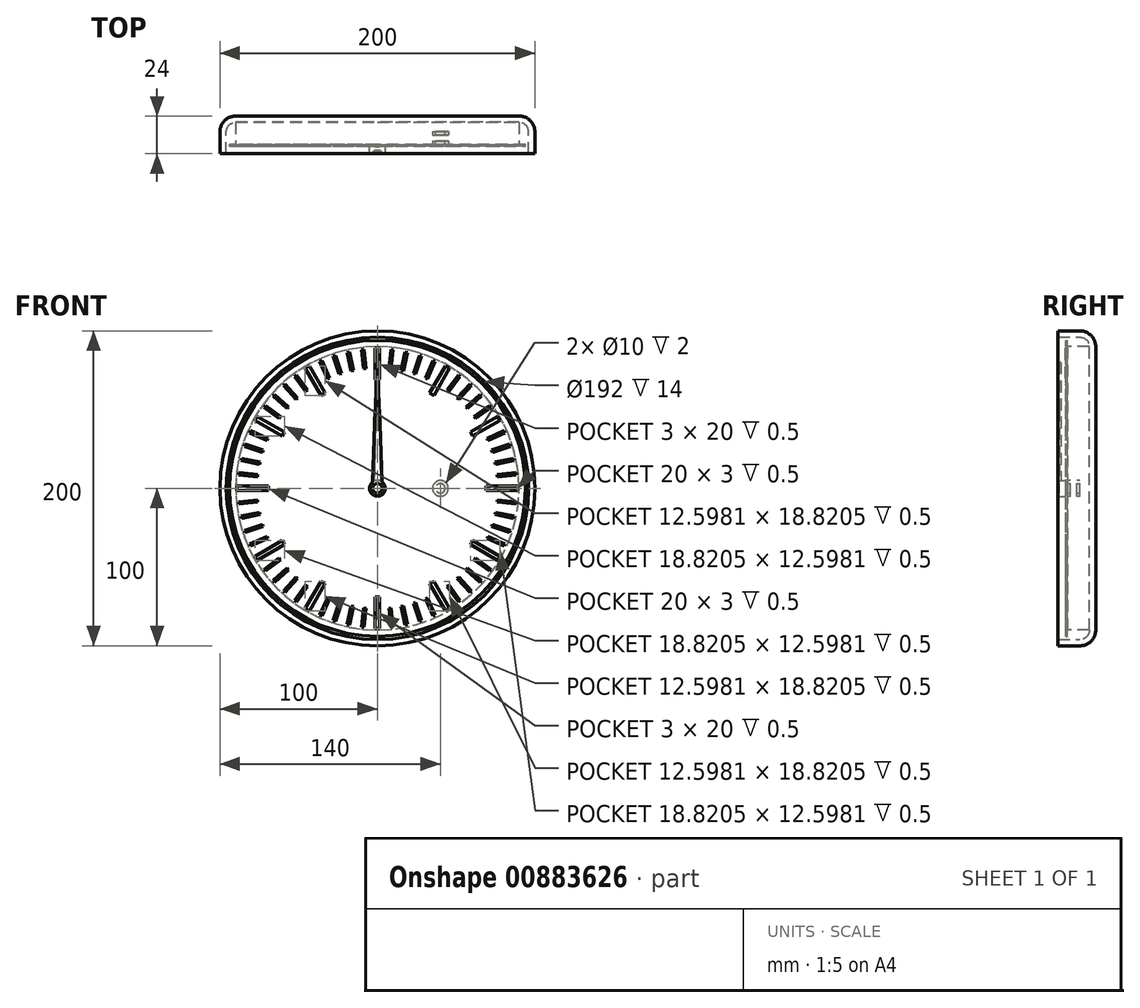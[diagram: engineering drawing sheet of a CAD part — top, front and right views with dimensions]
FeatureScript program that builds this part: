
annotation { "Feature Type Name" : "Feature", "Feature Type Description" : "" }
export const myFeature = defineFeature(function(context is Context, id is Id, definition is map)
    precondition{}
    {
        {
            var Q0;
            Q0=qCreatedBy(makeId("Front.planeOp"),FACE);
            var sketch = newSketch(context, id + "F0", { "sketchPlane" : qUnion([Q0])});
            skCircle(sketch, "E0", {"center": v(0, 0) * mm, "radius": 100 * mm});
            skSolve(sketch);
        }
        {
            var Q0;
            Q0 = qSketchRegion(id + "F0", true);
            extrude(context, id + "F1", {"entities" : qUnion([Q0]), "depth" : 24 * mm, "offsetDistance" : 25 * mm});
        }
        {
            var Q0;
            Q0=makeQuery(id+"F1.opExtrude","CAP_EDGE",EDGE,{"disambiguationData":[OSD([sQuery(id+"F0.wireOp",EDGE,"E0")])],"isStart":true});
            fillet(context, id + "F2", {"entities" : qUnion([Q0]), "radius" : 10 * mm, "tangentPropagation" : true, "allowEdgeOverflow" : false});
        }
        {
            var Q0;
            Q0=makeQuery(id+"F1.opExtrude","CAP_FACE",FACE,{"disambiguationData":[OSD([sQuery(id+"F0.wireOp",EDGE,"E0")])],"isStart":false});
            shell(context, id + "F3", {"entities" : qUnion([Q0]), "thickness" : 4 * mm});
        }
        {
            var Q0;
            {var subQ0=sQuery(id+"F0.wireOp",EDGE,"E0");Q0=makeQuery(id+"F3.opShell","OFFSET_FACE",FACE,{"disambiguationData":[OSD([subQ0]),TDD([makeQuery(id+"F1.opExtrude","CAP_FACE",FACE,{"disambiguationData":[OSD([subQ0])],"isStart":true})])]});}
            var sketch = newSketch(context, id + "F4", { "sketchPlane" : qUnion([Q0])});
            skCircle(sketch, "E1", {"center": v(0, 0) * mm, "radius": 5 * mm});
            skCircle(sketch, "E2", {"center": v(40, 0) * mm, "radius": 5 * mm});
            skCircle(sketch, "E3", {"center": v(0, 0) * mm, "radius": 3 * mm});
            skCircle(sketch, "E4", {"center": v(40, 0) * mm, "radius": 3 * mm});
            skSolve(sketch);
        }
        {
            var Q0;
            Q0 = qSketchRegion(id + "F4", true);
            extrude(context, id + "F5", {"entities" : qUnion([Q0]), "operationType" : NewBodyOperationType.ADD, "depth" : 2 * mm, "offsetDistance" : 25 * mm});
        }
        {
            var Q0;
            {var subQ0=sQuery(id+"F0.wireOp",EDGE,"E0");Q0=makeQuery(id+"F5.boolean.opBoolean","SPLIT",FACE,{"disambiguationData":[TD([makeQuery(id+"F5.opExtrude","SWEPT_FACE",FACE,{"disambiguationData":[OSD([sQuery(id+"F4.wireOp",EDGE,"E3")])]})])],"derivedFrom":makeQuery(id+"F3.opShell","OFFSET_FACE",FACE,{"disambiguationData":[OSD([subQ0]),TDD([makeQuery(id+"F1.opExtrude","CAP_FACE",FACE,{"disambiguationData":[OSD([subQ0])],"isStart":true})])]})});}
            extrude(context, id + "F6", {"entities" : qUnion([Q0]), "depth" : 19 * mm, "offsetDistance" : 25 * mm});
        }
        {
            var Q0;
            {var subQ0=sQuery(id+"F0.wireOp",EDGE,"E0");Q0=makeQuery(id+"F5.boolean.opBoolean","SPLIT",FACE,{"disambiguationData":[TD([makeQuery(id+"F5.opExtrude","SWEPT_FACE",FACE,{"disambiguationData":[OSD([sQuery(id+"F4.wireOp",EDGE,"E4")])]})])],"derivedFrom":makeQuery(id+"F3.opShell","OFFSET_FACE",FACE,{"disambiguationData":[OSD([subQ0]),TDD([makeQuery(id+"F1.opExtrude","CAP_FACE",FACE,{"disambiguationData":[OSD([subQ0])],"isStart":true})])]})});}
            extrude(context, id + "F7", {"entities" : qUnion([Q0]), "depth" : 8 * mm, "offsetDistance" : 25 * mm});
        }
        {
            var Q0;
            Q0=makeQuery(id+"F5.opExtrude","CAP_FACE",FACE,{"disambiguationData":[OSD([sQuery(id+"F4.wireOp",EDGE,"E1"),sQuery(id+"F4.wireOp",EDGE,"E3")])],"isStart":false});
            var sketch = newSketch(context, id + "F8", { "sketchPlane" : qUnion([Q0])});
            skCircle(sketch, "E5", {"center": v(0, 0) * mm, "radius": 9.38 * mm});
            skLineSegment(sketch, "E6", {"start": v(0, 11.38) * mm, "end": v(1.18, 11.38) * mm});
            skLineSegment(sketch, "E7", {"start": v(1.18, 11.38) * mm, "end": v(1.55, 9.25) * mm});
            skLineSegment(sketch, "E8.MirrorCS", {"start": v(0, 11.38) * mm, "end": v(-1.18, 11.38) * mm});
            skLineSegment(sketch, "E9.MirrorCS", {"start": v(-1.18, 11.38) * mm, "end": v(-1.55, 9.25) * mm});
            skLineSegment(sketch, "E10.1.0", {"start": v(-7.64, 8.51) * mm, "end": v(-6.7, 6.57) * mm});
            skLineSegment(sketch, "E10.1.1", {"start": v(-6.69, 9.2) * mm, "end": v(-7.64, 8.51) * mm});
            skLineSegment(sketch, "E10.1.2", {"start": v(-6.69, 9.2) * mm, "end": v(-5.73, 9.9) * mm});
            skLineSegment(sketch, "E10.1.3", {"start": v(-5.73, 9.9) * mm, "end": v(-4.18, 8.4) * mm});
            skLineSegment(sketch, "E10.2.0", {"start": v(-11.18, 2.4) * mm, "end": v(-9.27, 1.38) * mm});
            skLineSegment(sketch, "E10.2.1", {"start": v(-10.82, 3.52) * mm, "end": v(-11.18, 2.4) * mm});
            skLineSegment(sketch, "E10.2.2", {"start": v(-10.82, 3.52) * mm, "end": v(-10.45, 4.64) * mm});
            skLineSegment(sketch, "E10.2.3", {"start": v(-10.45, 4.64) * mm, "end": v(-8.31, 4.33) * mm});
            skLineSegment(sketch, "E11.2.3.0", {"start": v(-10.45, -4.64) * mm, "end": v(-8.31, -4.33) * mm});
            skLineSegment(sketch, "E11.3.3.0", {"start": v(-10.82, -3.52) * mm, "end": v(-10.45, -4.64) * mm});
            skLineSegment(sketch, "E11.6.3.0", {"start": v(-10.82, -3.52) * mm, "end": v(-11.18, -2.4) * mm});
            skLineSegment(sketch, "E11.9.3.0", {"start": v(-11.18, -2.4) * mm, "end": v(-9.27, -1.38) * mm});
            skLineSegment(sketch, "E11.2.4.0", {"start": v(-5.73, -9.9) * mm, "end": v(-4.18, -8.4) * mm});
            skLineSegment(sketch, "E11.3.4.0", {"start": v(-6.69, -9.2) * mm, "end": v(-5.73, -9.9) * mm});
            skLineSegment(sketch, "E11.6.4.0", {"start": v(-6.69, -9.2) * mm, "end": v(-7.64, -8.51) * mm});
            skLineSegment(sketch, "E11.9.4.0", {"start": v(-7.64, -8.51) * mm, "end": v(-6.7, -6.57) * mm});
            skLineSegment(sketch, "E11.2.5.0", {"start": v(1.18, -11.38) * mm, "end": v(1.55, -9.25) * mm});
            skLineSegment(sketch, "E11.3.5.0", {"start": v(0, -11.38) * mm, "end": v(1.18, -11.38) * mm});
            skLineSegment(sketch, "E11.6.5.0", {"start": v(0, -11.38) * mm, "end": v(-1.18, -11.38) * mm});
            skLineSegment(sketch, "E11.9.5.0", {"start": v(-1.18, -11.38) * mm, "end": v(-1.55, -9.25) * mm});
            skLineSegment(sketch, "E11.2.6.0", {"start": v(7.64, -8.51) * mm, "end": v(6.7, -6.57) * mm});
            skLineSegment(sketch, "E11.3.6.0", {"start": v(6.69, -9.2) * mm, "end": v(7.64, -8.51) * mm});
            skLineSegment(sketch, "E11.6.6.0", {"start": v(6.69, -9.2) * mm, "end": v(5.73, -9.9) * mm});
            skLineSegment(sketch, "E11.9.6.0", {"start": v(5.73, -9.9) * mm, "end": v(4.18, -8.4) * mm});
            skLineSegment(sketch, "E11.2.7.0", {"start": v(11.18, -2.4) * mm, "end": v(9.27, -1.38) * mm});
            skLineSegment(sketch, "E11.3.7.0", {"start": v(10.82, -3.52) * mm, "end": v(11.18, -2.4) * mm});
            skLineSegment(sketch, "E11.6.7.0", {"start": v(10.82, -3.52) * mm, "end": v(10.45, -4.64) * mm});
            skLineSegment(sketch, "E11.9.7.0", {"start": v(10.45, -4.64) * mm, "end": v(8.31, -4.33) * mm});
            skLineSegment(sketch, "E11.2.8.0", {"start": v(10.45, 4.64) * mm, "end": v(8.31, 4.33) * mm});
            skLineSegment(sketch, "E11.3.8.0", {"start": v(10.82, 3.52) * mm, "end": v(10.45, 4.64) * mm});
            skLineSegment(sketch, "E11.6.8.0", {"start": v(10.82, 3.52) * mm, "end": v(11.18, 2.4) * mm});
            skLineSegment(sketch, "E11.9.8.0", {"start": v(11.18, 2.4) * mm, "end": v(9.27, 1.38) * mm});
            skLineSegment(sketch, "E11.2.9.0", {"start": v(5.73, 9.9) * mm, "end": v(4.18, 8.4) * mm});
            skLineSegment(sketch, "E11.3.9.0", {"start": v(6.69, 9.2) * mm, "end": v(5.73, 9.9) * mm});
            skLineSegment(sketch, "E11.6.9.0", {"start": v(6.69, 9.2) * mm, "end": v(7.64, 8.51) * mm});
            skLineSegment(sketch, "E11.9.9.0", {"start": v(7.64, 8.51) * mm, "end": v(6.7, 6.57) * mm});
            skSolve(sketch);
        }
        {
            var Q0;
            Q0 = qSketchRegion(id + "F8", true);
            extrude(context, id + "F9", {"entities" : qUnion([Q0]), "operationType" : NewBodyOperationType.ADD, "depth" : 4 * mm, "offsetDistance" : 25 * mm});
        }
        {
            var Q0;
            Q0=makeQuery(id+"F5.opExtrude","CAP_FACE",FACE,{"disambiguationData":[OSD([sQuery(id+"F4.wireOp",EDGE,"E2"),sQuery(id+"F4.wireOp",EDGE,"E4")])],"isStart":false});
            var sketch = newSketch(context, id + "F10", { "sketchPlane" : qUnion([Q0])});
            skCircle(sketch, "E12", {"center": v(40, 0) * mm, "radius": 28.12 * mm});
            skLineSegment(sketch, "E13", {"start": v(9.88, 0) * mm, "end": v(9.88, 1.18) * mm});
            skLineSegment(sketch, "E14", {"start": v(9.88, 1.18) * mm, "end": v(11.92, 1.54) * mm});
            skLineSegment(sketch, "E15.MirrorCS", {"start": v(9.88, 0) * mm, "end": v(9.88, -1.18) * mm});
            skLineSegment(sketch, "E16.MirrorCS", {"start": v(9.88, -1.18) * mm, "end": v(11.92, -1.54) * mm});
            skLineSegment(sketch, "E17.1.0", {"start": v(10.78, -7.42) * mm, "end": v(12.85, -7.34) * mm});
            skLineSegment(sketch, "E17.1.1", {"start": v(10.53, -6.26) * mm, "end": v(10.78, -7.42) * mm});
            skLineSegment(sketch, "E17.1.2", {"start": v(10.53, -6.26) * mm, "end": v(10.29, -5.11) * mm});
            skLineSegment(sketch, "E17.1.3", {"start": v(10.29, -5.11) * mm, "end": v(12.21, -4.33) * mm});
            skLineSegment(sketch, "E17.2.0", {"start": v(12.96, -13.33) * mm, "end": v(14.97, -12.83) * mm});
            skLineSegment(sketch, "E17.2.1", {"start": v(12.48, -12.25) * mm, "end": v(12.96, -13.33) * mm});
            skLineSegment(sketch, "E17.2.2", {"start": v(12.48, -12.25) * mm, "end": v(12, -11.18) * mm});
            skLineSegment(sketch, "E17.2.3", {"start": v(12, -11.18) * mm, "end": v(13.72, -10.02) * mm});
            skLineSegment(sketch, "E18.1.3.0", {"start": v(16.32, -18.66) * mm, "end": v(18.18, -17.75) * mm});
            skLineSegment(sketch, "E18.3.3.0", {"start": v(15.63, -17.7) * mm, "end": v(16.32, -18.66) * mm});
            skLineSegment(sketch, "E18.6.3.0", {"start": v(15.63, -17.7) * mm, "end": v(14.94, -16.75) * mm});
            skLineSegment(sketch, "E18.9.3.0", {"start": v(14.94, -16.75) * mm, "end": v(16.38, -15.26) * mm});
            skLineSegment(sketch, "E18.1.4.0", {"start": v(20.72, -23.18) * mm, "end": v(22.35, -21.9) * mm});
            skLineSegment(sketch, "E18.3.4.0", {"start": v(19.84, -22.39) * mm, "end": v(20.72, -23.18) * mm});
            skLineSegment(sketch, "E18.6.4.0", {"start": v(19.84, -22.39) * mm, "end": v(18.97, -21.6) * mm});
            skLineSegment(sketch, "E18.9.4.0", {"start": v(18.97, -21.6) * mm, "end": v(20.07, -19.84) * mm});
            skLineSegment(sketch, "E18.1.5.0", {"start": v(25.96, -26.68) * mm, "end": v(27.3, -25.09) * mm});
            skLineSegment(sketch, "E18.3.5.0", {"start": v(24.94, -26.09) * mm, "end": v(25.96, -26.68) * mm});
            skLineSegment(sketch, "E18.6.5.0", {"start": v(24.94, -26.09) * mm, "end": v(23.92, -25.5) * mm});
            skLineSegment(sketch, "E18.9.5.0", {"start": v(23.92, -25.5) * mm, "end": v(24.63, -23.55) * mm});
            skLineSegment(sketch, "E18.1.6.0", {"start": v(31.81, -29.01) * mm, "end": v(32.78, -27.18) * mm});
            skLineSegment(sketch, "E18.3.6.0", {"start": v(30.7, -28.65) * mm, "end": v(31.81, -29.01) * mm});
            skLineSegment(sketch, "E18.6.6.0", {"start": v(30.7, -28.65) * mm, "end": v(29.57, -28.29) * mm});
            skLineSegment(sketch, "E18.9.6.0", {"start": v(29.57, -28.29) * mm, "end": v(29.86, -26.23) * mm});
            skLineSegment(sketch, "E18.1.7.0", {"start": v(38.02, -30.08) * mm, "end": v(38.6, -28.09) * mm});
            skLineSegment(sketch, "E18.3.7.0", {"start": v(36.85, -29.96) * mm, "end": v(38.02, -30.08) * mm});
            skLineSegment(sketch, "E18.6.7.0", {"start": v(36.85, -29.96) * mm, "end": v(35.68, -29.84) * mm});
            skLineSegment(sketch, "E18.9.7.0", {"start": v(35.68, -29.84) * mm, "end": v(35.53, -27.77) * mm});
            skLineSegment(sketch, "E18.1.8.0", {"start": v(44.32, -29.84) * mm, "end": v(44.47, -27.77) * mm});
            skLineSegment(sketch, "E18.3.8.0", {"start": v(43.15, -29.96) * mm, "end": v(44.32, -29.84) * mm});
            skLineSegment(sketch, "E18.6.8.0", {"start": v(43.15, -29.96) * mm, "end": v(41.98, -30.08) * mm});
            skLineSegment(sketch, "E18.9.8.0", {"start": v(41.98, -30.08) * mm, "end": v(41.4, -28.09) * mm});
            skLineSegment(sketch, "E18.1.9.0", {"start": v(50.43, -28.29) * mm, "end": v(50.14, -26.23) * mm});
            skLineSegment(sketch, "E18.3.9.0", {"start": v(49.3, -28.65) * mm, "end": v(50.43, -28.29) * mm});
            skLineSegment(sketch, "E18.6.9.0", {"start": v(49.3, -28.65) * mm, "end": v(48.19, -29.01) * mm});
            skLineSegment(sketch, "E18.9.9.0", {"start": v(48.19, -29.01) * mm, "end": v(47.22, -27.18) * mm});
            skLineSegment(sketch, "E18.1.10.0", {"start": v(56.08, -25.5) * mm, "end": v(55.37, -23.55) * mm});
            skLineSegment(sketch, "E18.3.10.0", {"start": v(55.06, -26.09) * mm, "end": v(56.08, -25.5) * mm});
            skLineSegment(sketch, "E18.6.10.0", {"start": v(55.06, -26.09) * mm, "end": v(54.04, -26.68) * mm});
            skLineSegment(sketch, "E18.9.10.0", {"start": v(54.04, -26.68) * mm, "end": v(52.7, -25.09) * mm});
            skLineSegment(sketch, "E18.1.11.0", {"start": v(61.03, -21.6) * mm, "end": v(59.93, -19.84) * mm});
            skLineSegment(sketch, "E18.3.11.0", {"start": v(60.16, -22.39) * mm, "end": v(61.03, -21.6) * mm});
            skLineSegment(sketch, "E18.6.11.0", {"start": v(60.16, -22.39) * mm, "end": v(59.28, -23.18) * mm});
            skLineSegment(sketch, "E18.9.11.0", {"start": v(59.28, -23.18) * mm, "end": v(57.65, -21.9) * mm});
            skLineSegment(sketch, "E18.1.12.0", {"start": v(65.06, -16.75) * mm, "end": v(63.62, -15.26) * mm});
            skLineSegment(sketch, "E18.3.12.0", {"start": v(64.37, -17.7) * mm, "end": v(65.06, -16.75) * mm});
            skLineSegment(sketch, "E18.6.12.0", {"start": v(64.37, -17.7) * mm, "end": v(63.68, -18.66) * mm});
            skLineSegment(sketch, "E18.9.12.0", {"start": v(63.68, -18.66) * mm, "end": v(61.82, -17.75) * mm});
            skLineSegment(sketch, "E18.1.13.0", {"start": v(68, -11.18) * mm, "end": v(66.28, -10.02) * mm});
            skLineSegment(sketch, "E18.3.13.0", {"start": v(67.52, -12.25) * mm, "end": v(68, -11.18) * mm});
            skLineSegment(sketch, "E18.6.13.0", {"start": v(67.52, -12.25) * mm, "end": v(67.04, -13.33) * mm});
            skLineSegment(sketch, "E18.9.13.0", {"start": v(67.04, -13.33) * mm, "end": v(65.03, -12.83) * mm});
            skLineSegment(sketch, "E18.1.14.0", {"start": v(69.71, -5.11) * mm, "end": v(67.79, -4.33) * mm});
            skLineSegment(sketch, "E18.3.14.0", {"start": v(69.47, -6.26) * mm, "end": v(69.71, -5.11) * mm});
            skLineSegment(sketch, "E18.6.14.0", {"start": v(69.47, -6.26) * mm, "end": v(69.22, -7.42) * mm});
            skLineSegment(sketch, "E18.9.14.0", {"start": v(69.22, -7.42) * mm, "end": v(67.15, -7.34) * mm});
            skLineSegment(sketch, "E18.1.15.0", {"start": v(70.13, 1.18) * mm, "end": v(68.08, 1.54) * mm});
            skLineSegment(sketch, "E18.3.15.0", {"start": v(70.12, 0) * mm, "end": v(70.12, 1.18) * mm});
            skLineSegment(sketch, "E18.6.15.0", {"start": v(70.12, 0) * mm, "end": v(70.12, -1.18) * mm});
            skLineSegment(sketch, "E18.9.15.0", {"start": v(70.13, -1.18) * mm, "end": v(68.08, -1.54) * mm});
            skLineSegment(sketch, "E18.1.16.0", {"start": v(69.22, 7.42) * mm, "end": v(67.15, 7.34) * mm});
            skLineSegment(sketch, "E18.3.16.0", {"start": v(69.47, 6.26) * mm, "end": v(69.22, 7.42) * mm});
            skLineSegment(sketch, "E18.6.16.0", {"start": v(69.47, 6.26) * mm, "end": v(69.71, 5.11) * mm});
            skLineSegment(sketch, "E18.9.16.0", {"start": v(69.71, 5.11) * mm, "end": v(67.79, 4.33) * mm});
            skLineSegment(sketch, "E18.1.17.0", {"start": v(67.04, 13.33) * mm, "end": v(65.03, 12.83) * mm});
            skLineSegment(sketch, "E18.3.17.0", {"start": v(67.52, 12.25) * mm, "end": v(67.04, 13.33) * mm});
            skLineSegment(sketch, "E18.6.17.0", {"start": v(67.52, 12.25) * mm, "end": v(68, 11.18) * mm});
            skLineSegment(sketch, "E18.9.17.0", {"start": v(68, 11.18) * mm, "end": v(66.28, 10.02) * mm});
            skLineSegment(sketch, "E18.1.18.0", {"start": v(63.68, 18.66) * mm, "end": v(61.82, 17.75) * mm});
            skLineSegment(sketch, "E18.3.18.0", {"start": v(64.37, 17.7) * mm, "end": v(63.68, 18.66) * mm});
            skLineSegment(sketch, "E18.6.18.0", {"start": v(64.37, 17.7) * mm, "end": v(65.06, 16.75) * mm});
            skLineSegment(sketch, "E18.9.18.0", {"start": v(65.06, 16.75) * mm, "end": v(63.62, 15.26) * mm});
            skLineSegment(sketch, "E18.1.19.0", {"start": v(59.28, 23.18) * mm, "end": v(57.65, 21.9) * mm});
            skLineSegment(sketch, "E18.3.19.0", {"start": v(60.16, 22.39) * mm, "end": v(59.28, 23.18) * mm});
            skLineSegment(sketch, "E18.6.19.0", {"start": v(60.16, 22.39) * mm, "end": v(61.03, 21.6) * mm});
            skLineSegment(sketch, "E18.9.19.0", {"start": v(61.03, 21.6) * mm, "end": v(59.93, 19.84) * mm});
            skLineSegment(sketch, "E18.1.20.0", {"start": v(54.04, 26.68) * mm, "end": v(52.7, 25.09) * mm});
            skLineSegment(sketch, "E18.3.20.0", {"start": v(55.06, 26.09) * mm, "end": v(54.04, 26.68) * mm});
            skLineSegment(sketch, "E18.6.20.0", {"start": v(55.06, 26.09) * mm, "end": v(56.08, 25.5) * mm});
            skLineSegment(sketch, "E18.9.20.0", {"start": v(56.08, 25.5) * mm, "end": v(55.37, 23.55) * mm});
            skLineSegment(sketch, "E18.1.21.0", {"start": v(48.19, 29.01) * mm, "end": v(47.22, 27.18) * mm});
            skLineSegment(sketch, "E18.3.21.0", {"start": v(49.3, 28.65) * mm, "end": v(48.19, 29.01) * mm});
            skLineSegment(sketch, "E18.6.21.0", {"start": v(49.3, 28.65) * mm, "end": v(50.43, 28.29) * mm});
            skLineSegment(sketch, "E18.9.21.0", {"start": v(50.43, 28.29) * mm, "end": v(50.14, 26.23) * mm});
            skLineSegment(sketch, "E18.1.22.0", {"start": v(41.98, 30.08) * mm, "end": v(41.4, 28.09) * mm});
            skLineSegment(sketch, "E18.3.22.0", {"start": v(43.15, 29.96) * mm, "end": v(41.98, 30.08) * mm});
            skLineSegment(sketch, "E18.6.22.0", {"start": v(43.15, 29.96) * mm, "end": v(44.32, 29.84) * mm});
            skLineSegment(sketch, "E18.9.22.0", {"start": v(44.32, 29.84) * mm, "end": v(44.47, 27.77) * mm});
            skLineSegment(sketch, "E18.1.23.0", {"start": v(35.68, 29.84) * mm, "end": v(35.53, 27.77) * mm});
            skLineSegment(sketch, "E18.3.23.0", {"start": v(36.85, 29.96) * mm, "end": v(35.68, 29.84) * mm});
            skLineSegment(sketch, "E18.6.23.0", {"start": v(36.85, 29.96) * mm, "end": v(38.02, 30.08) * mm});
            skLineSegment(sketch, "E18.9.23.0", {"start": v(38.02, 30.08) * mm, "end": v(38.6, 28.09) * mm});
            skLineSegment(sketch, "E18.1.24.0", {"start": v(29.57, 28.29) * mm, "end": v(29.86, 26.23) * mm});
            skLineSegment(sketch, "E18.3.24.0", {"start": v(30.7, 28.65) * mm, "end": v(29.57, 28.29) * mm});
            skLineSegment(sketch, "E18.6.24.0", {"start": v(30.7, 28.65) * mm, "end": v(31.81, 29.01) * mm});
            skLineSegment(sketch, "E18.9.24.0", {"start": v(31.81, 29.01) * mm, "end": v(32.78, 27.18) * mm});
            skLineSegment(sketch, "E18.1.25.0", {"start": v(23.92, 25.5) * mm, "end": v(24.63, 23.55) * mm});
            skLineSegment(sketch, "E18.3.25.0", {"start": v(24.94, 26.09) * mm, "end": v(23.92, 25.5) * mm});
            skLineSegment(sketch, "E18.6.25.0", {"start": v(24.94, 26.09) * mm, "end": v(25.96, 26.68) * mm});
            skLineSegment(sketch, "E18.9.25.0", {"start": v(25.96, 26.68) * mm, "end": v(27.3, 25.09) * mm});
            skLineSegment(sketch, "E18.1.26.0", {"start": v(18.97, 21.6) * mm, "end": v(20.07, 19.84) * mm});
            skLineSegment(sketch, "E18.3.26.0", {"start": v(19.84, 22.39) * mm, "end": v(18.97, 21.6) * mm});
            skLineSegment(sketch, "E18.6.26.0", {"start": v(19.84, 22.39) * mm, "end": v(20.72, 23.18) * mm});
            skLineSegment(sketch, "E18.9.26.0", {"start": v(20.72, 23.18) * mm, "end": v(22.35, 21.9) * mm});
            skLineSegment(sketch, "E18.1.27.0", {"start": v(14.94, 16.75) * mm, "end": v(16.38, 15.26) * mm});
            skLineSegment(sketch, "E18.3.27.0", {"start": v(15.63, 17.7) * mm, "end": v(14.94, 16.75) * mm});
            skLineSegment(sketch, "E18.6.27.0", {"start": v(15.63, 17.7) * mm, "end": v(16.32, 18.66) * mm});
            skLineSegment(sketch, "E18.9.27.0", {"start": v(16.32, 18.66) * mm, "end": v(18.18, 17.75) * mm});
            skLineSegment(sketch, "E18.1.28.0", {"start": v(12, 11.18) * mm, "end": v(13.72, 10.02) * mm});
            skLineSegment(sketch, "E18.3.28.0", {"start": v(12.48, 12.25) * mm, "end": v(12, 11.18) * mm});
            skLineSegment(sketch, "E18.6.28.0", {"start": v(12.48, 12.25) * mm, "end": v(12.96, 13.33) * mm});
            skLineSegment(sketch, "E18.9.28.0", {"start": v(12.96, 13.33) * mm, "end": v(14.97, 12.83) * mm});
            skLineSegment(sketch, "E18.1.29.0", {"start": v(10.29, 5.11) * mm, "end": v(12.21, 4.33) * mm});
            skLineSegment(sketch, "E18.3.29.0", {"start": v(10.53, 6.26) * mm, "end": v(10.29, 5.11) * mm});
            skLineSegment(sketch, "E18.6.29.0", {"start": v(10.53, 6.26) * mm, "end": v(10.78, 7.42) * mm});
            skLineSegment(sketch, "E18.9.29.0", {"start": v(10.78, 7.42) * mm, "end": v(12.85, 7.34) * mm});
            skSolve(sketch);
        }
        {
            var Q0;
            Q0 = qSketchRegion(id + "F10", true);
            extrude(context, id + "F11", {"entities" : qUnion([Q0]), "operationType" : NewBodyOperationType.ADD, "depth" : 4 * mm, "offsetDistance" : 25 * mm});
        }
        {
            var Q0;
            Q0=makeQuery(id+"F9.opExtrude","CAP_FACE",FACE,{"disambiguationData":[OSD([sQuery(id+"F8.wireOp",EDGE,"E5"),sQuery(id+"F8.wireOp",EDGE,"E6"),sQuery(id+"F8.wireOp",EDGE,"E7"),sQuery(id+"F8.wireOp",EDGE,"E8.MirrorCS"),sQuery(id+"F8.wireOp",EDGE,"E9.MirrorCS"),sQuery(id+"F8.wireOp",EDGE,"E10.1.0"),sQuery(id+"F8.wireOp",EDGE,"E10.1.1"),sQuery(id+"F8.wireOp",EDGE,"E10.1.2"),sQuery(id+"F8.wireOp",EDGE,"E10.1.3"),sQuery(id+"F8.wireOp",EDGE,"E10.2.0"),sQuery(id+"F8.wireOp",EDGE,"E10.2.1"),sQuery(id+"F8.wireOp",EDGE,"E10.2.2"),sQuery(id+"F8.wireOp",EDGE,"E10.2.3"),sQuery(id+"F8.wireOp",EDGE,"E11.2.3.0"),sQuery(id+"F8.wireOp",EDGE,"E11.3.3.0"),sQuery(id+"F8.wireOp",EDGE,"E11.6.3.0"),sQuery(id+"F8.wireOp",EDGE,"E11.9.3.0"),sQuery(id+"F8.wireOp",EDGE,"E11.2.4.0"),sQuery(id+"F8.wireOp",EDGE,"E11.3.4.0"),sQuery(id+"F8.wireOp",EDGE,"E11.6.4.0"),sQuery(id+"F8.wireOp",EDGE,"E11.9.4.0"),sQuery(id+"F8.wireOp",EDGE,"E11.2.5.0"),sQuery(id+"F8.wireOp",EDGE,"E11.3.5.0"),sQuery(id+"F8.wireOp",EDGE,"E11.6.5.0"),sQuery(id+"F8.wireOp",EDGE,"E11.9.5.0"),sQuery(id+"F8.wireOp",EDGE,"E11.2.6.0"),sQuery(id+"F8.wireOp",EDGE,"E11.3.6.0"),sQuery(id+"F8.wireOp",EDGE,"E11.6.6.0"),sQuery(id+"F8.wireOp",EDGE,"E11.9.6.0"),sQuery(id+"F8.wireOp",EDGE,"E11.2.7.0"),sQuery(id+"F8.wireOp",EDGE,"E11.3.7.0"),sQuery(id+"F8.wireOp",EDGE,"E11.6.7.0"),sQuery(id+"F8.wireOp",EDGE,"E11.9.7.0"),sQuery(id+"F8.wireOp",EDGE,"E11.2.8.0"),sQuery(id+"F8.wireOp",EDGE,"E11.3.8.0"),sQuery(id+"F8.wireOp",EDGE,"E11.6.8.0"),sQuery(id+"F8.wireOp",EDGE,"E11.9.8.0"),sQuery(id+"F8.wireOp",EDGE,"E11.2.9.0"),sQuery(id+"F8.wireOp",EDGE,"E11.3.9.0"),sQuery(id+"F8.wireOp",EDGE,"E11.6.9.0"),sQuery(id+"F8.wireOp",EDGE,"E11.9.9.0")])],"isStart":false});
            var sketch = newSketch(context, id + "F12", { "sketchPlane" : qUnion([Q0])});
            skCircle(sketch, "E19.0", {"center": v(0, 0) * mm, "radius": 5 * mm});
            skCircle(sketch, "E19.1.0", {"center": v(0, 0) * mm, "radius": 3 * mm});
            skSolve(sketch);
        }
        {
            var Q0;
            Q0 = qSketchRegion(id + "F12", true);
            extrude(context, id + "F13", {"entities" : qUnion([Q0]), "depth" : 2 * mm, "offsetDistance" : 25 * mm});
        }
        {
            var Q0;
            Q0=makeQuery(id+"F13.opExtrude","CAP_FACE",FACE,{"disambiguationData":[OSD([sQuery(id+"F12.wireOp",EDGE,"E19.0"),sQuery(id+"F12.wireOp",EDGE,"E19.1.0")])],"isStart":false});
            var sketch = newSketch(context, id + "F14", { "sketchPlane" : qUnion([Q0])});
            skCircle(sketch, "E20", {"center": v(0, 0) * mm, "radius": 30 * mm});
            skLineSegment(sketch, "E21", {"start": v(0, 32) * mm, "end": v(0.94, 32) * mm});
            skLineSegment(sketch, "E22", {"start": v(0.94, 32) * mm, "end": v(1.3, 29.97) * mm});
            skLineSegment(sketch, "E23.MirrorCS", {"start": v(0, 32) * mm, "end": v(-0.94, 32) * mm});
            skLineSegment(sketch, "E24.MirrorCS", {"start": v(-0.94, 32) * mm, "end": v(-1.3, 29.97) * mm});
            skLineSegment(sketch, "E25.1.0", {"start": v(-5.94, 31.46) * mm, "end": v(-5.97, 29.4) * mm});
            skLineSegment(sketch, "E25.1.1", {"start": v(-5, 31.6) * mm, "end": v(-5.94, 31.46) * mm});
            skLineSegment(sketch, "E25.1.2", {"start": v(-5, 31.6) * mm, "end": v(-4.08, 31.75) * mm});
            skLineSegment(sketch, "E25.1.3", {"start": v(-4.08, 31.75) * mm, "end": v(-3.4, 29.8) * mm});
            skLineSegment(sketch, "E25.2.0", {"start": v(-10.78, 30.14) * mm, "end": v(-10.5, 28.1) * mm});
            skLineSegment(sketch, "E25.2.1", {"start": v(-9.89, 30.43) * mm, "end": v(-10.78, 30.14) * mm});
            skLineSegment(sketch, "E25.2.2", {"start": v(-9.89, 30.43) * mm, "end": v(-9, 30.73) * mm});
            skLineSegment(sketch, "E25.2.3", {"start": v(-9, 30.73) * mm, "end": v(-8.03, 28.9) * mm});
            skLineSegment(sketch, "E26.2.3.0", {"start": v(-15.37, 28.08) * mm, "end": v(-14.77, 26.11) * mm});
            skLineSegment(sketch, "E26.3.3.0", {"start": v(-14.53, 28.51) * mm, "end": v(-15.37, 28.08) * mm});
            skLineSegment(sketch, "E26.6.3.0", {"start": v(-14.53, 28.51) * mm, "end": v(-13.69, 28.94) * mm});
            skLineSegment(sketch, "E26.9.3.0", {"start": v(-13.69, 28.94) * mm, "end": v(-12.45, 27.3) * mm});
            skLineSegment(sketch, "E26.2.4.0", {"start": v(-19.57, 25.33) * mm, "end": v(-18.67, 23.48) * mm});
            skLineSegment(sketch, "E26.3.4.0", {"start": v(-18.8, 25.89) * mm, "end": v(-19.57, 25.33) * mm});
            skLineSegment(sketch, "E26.6.4.0", {"start": v(-18.8, 25.89) * mm, "end": v(-18.05, 26.44) * mm});
            skLineSegment(sketch, "E26.9.4.0", {"start": v(-18.05, 26.44) * mm, "end": v(-16.57, 25.01) * mm});
            skLineSegment(sketch, "E26.2.5.0", {"start": v(-23.3, 21.96) * mm, "end": v(-22.11, 20.27) * mm});
            skLineSegment(sketch, "E26.3.5.0", {"start": v(-22.63, 22.63) * mm, "end": v(-23.3, 21.96) * mm});
            skLineSegment(sketch, "E26.6.5.0", {"start": v(-22.63, 22.63) * mm, "end": v(-21.96, 23.3) * mm});
            skLineSegment(sketch, "E26.9.5.0", {"start": v(-21.96, 23.3) * mm, "end": v(-20.27, 22.11) * mm});
            skLineSegment(sketch, "E26.2.6.0", {"start": v(-26.44, 18.05) * mm, "end": v(-25.01, 16.57) * mm});
            skLineSegment(sketch, "E26.3.6.0", {"start": v(-25.89, 18.8) * mm, "end": v(-26.44, 18.05) * mm});
            skLineSegment(sketch, "E26.6.6.0", {"start": v(-25.89, 18.8) * mm, "end": v(-25.33, 19.57) * mm});
            skLineSegment(sketch, "E26.9.6.0", {"start": v(-25.33, 19.57) * mm, "end": v(-23.48, 18.67) * mm});
            skLineSegment(sketch, "E26.2.7.0", {"start": v(-28.94, 13.69) * mm, "end": v(-27.3, 12.45) * mm});
            skLineSegment(sketch, "E26.3.7.0", {"start": v(-28.51, 14.53) * mm, "end": v(-28.94, 13.69) * mm});
            skLineSegment(sketch, "E26.6.7.0", {"start": v(-28.51, 14.53) * mm, "end": v(-28.08, 15.37) * mm});
            skLineSegment(sketch, "E26.9.7.0", {"start": v(-28.08, 15.37) * mm, "end": v(-26.11, 14.77) * mm});
            skLineSegment(sketch, "E26.2.8.0", {"start": v(-30.73, 9) * mm, "end": v(-28.9, 8.03) * mm});
            skLineSegment(sketch, "E26.3.8.0", {"start": v(-30.43, 9.89) * mm, "end": v(-30.73, 9) * mm});
            skLineSegment(sketch, "E26.6.8.0", {"start": v(-30.43, 9.89) * mm, "end": v(-30.14, 10.78) * mm});
            skLineSegment(sketch, "E26.9.8.0", {"start": v(-30.14, 10.78) * mm, "end": v(-28.1, 10.5) * mm});
            skLineSegment(sketch, "E26.2.9.0", {"start": v(-31.75, 4.08) * mm, "end": v(-29.8, 3.4) * mm});
            skLineSegment(sketch, "E26.3.9.0", {"start": v(-31.6, 5) * mm, "end": v(-31.75, 4.08) * mm});
            skLineSegment(sketch, "E26.6.9.0", {"start": v(-31.6, 5) * mm, "end": v(-31.46, 5.94) * mm});
            skLineSegment(sketch, "E26.9.9.0", {"start": v(-31.46, 5.94) * mm, "end": v(-29.4, 5.97) * mm});
            skLineSegment(sketch, "E26.2.10.0", {"start": v(-32, -0.94) * mm, "end": v(-29.97, -1.3) * mm});
            skLineSegment(sketch, "E26.3.10.0", {"start": v(-32, 0) * mm, "end": v(-32, -0.94) * mm});
            skLineSegment(sketch, "E26.6.10.0", {"start": v(-32, 0) * mm, "end": v(-32, 0.94) * mm});
            skLineSegment(sketch, "E26.9.10.0", {"start": v(-32, 0.94) * mm, "end": v(-29.97, 1.3) * mm});
            skLineSegment(sketch, "E26.2.11.0", {"start": v(-31.46, -5.94) * mm, "end": v(-29.4, -5.97) * mm});
            skLineSegment(sketch, "E26.3.11.0", {"start": v(-31.6, -5) * mm, "end": v(-31.46, -5.94) * mm});
            skLineSegment(sketch, "E26.6.11.0", {"start": v(-31.6, -5) * mm, "end": v(-31.75, -4.08) * mm});
            skLineSegment(sketch, "E26.9.11.0", {"start": v(-31.75, -4.08) * mm, "end": v(-29.8, -3.4) * mm});
            skLineSegment(sketch, "E26.2.12.0", {"start": v(-30.14, -10.78) * mm, "end": v(-28.1, -10.5) * mm});
            skLineSegment(sketch, "E26.3.12.0", {"start": v(-30.43, -9.89) * mm, "end": v(-30.14, -10.78) * mm});
            skLineSegment(sketch, "E26.6.12.0", {"start": v(-30.43, -9.89) * mm, "end": v(-30.73, -9) * mm});
            skLineSegment(sketch, "E26.9.12.0", {"start": v(-30.73, -9) * mm, "end": v(-28.9, -8.03) * mm});
            skLineSegment(sketch, "E26.2.13.0", {"start": v(-28.08, -15.37) * mm, "end": v(-26.11, -14.77) * mm});
            skLineSegment(sketch, "E26.3.13.0", {"start": v(-28.51, -14.53) * mm, "end": v(-28.08, -15.37) * mm});
            skLineSegment(sketch, "E26.6.13.0", {"start": v(-28.51, -14.53) * mm, "end": v(-28.94, -13.69) * mm});
            skLineSegment(sketch, "E26.9.13.0", {"start": v(-28.94, -13.69) * mm, "end": v(-27.3, -12.45) * mm});
            skLineSegment(sketch, "E26.2.14.0", {"start": v(-25.33, -19.57) * mm, "end": v(-23.48, -18.67) * mm});
            skLineSegment(sketch, "E26.3.14.0", {"start": v(-25.89, -18.8) * mm, "end": v(-25.33, -19.57) * mm});
            skLineSegment(sketch, "E26.6.14.0", {"start": v(-25.89, -18.8) * mm, "end": v(-26.44, -18.05) * mm});
            skLineSegment(sketch, "E26.9.14.0", {"start": v(-26.44, -18.05) * mm, "end": v(-25.01, -16.57) * mm});
            skLineSegment(sketch, "E26.2.15.0", {"start": v(-21.96, -23.3) * mm, "end": v(-20.27, -22.11) * mm});
            skLineSegment(sketch, "E26.3.15.0", {"start": v(-22.63, -22.63) * mm, "end": v(-21.96, -23.3) * mm});
            skLineSegment(sketch, "E26.6.15.0", {"start": v(-22.63, -22.63) * mm, "end": v(-23.3, -21.96) * mm});
            skLineSegment(sketch, "E26.9.15.0", {"start": v(-23.3, -21.96) * mm, "end": v(-22.11, -20.27) * mm});
            skLineSegment(sketch, "E26.2.16.0", {"start": v(-18.05, -26.44) * mm, "end": v(-16.57, -25.01) * mm});
            skLineSegment(sketch, "E26.3.16.0", {"start": v(-18.8, -25.89) * mm, "end": v(-18.05, -26.44) * mm});
            skLineSegment(sketch, "E26.6.16.0", {"start": v(-18.8, -25.89) * mm, "end": v(-19.57, -25.33) * mm});
            skLineSegment(sketch, "E26.9.16.0", {"start": v(-19.57, -25.33) * mm, "end": v(-18.67, -23.48) * mm});
            skLineSegment(sketch, "E26.2.17.0", {"start": v(-13.69, -28.94) * mm, "end": v(-12.45, -27.3) * mm});
            skLineSegment(sketch, "E26.3.17.0", {"start": v(-14.53, -28.51) * mm, "end": v(-13.69, -28.94) * mm});
            skLineSegment(sketch, "E26.6.17.0", {"start": v(-14.53, -28.51) * mm, "end": v(-15.37, -28.08) * mm});
            skLineSegment(sketch, "E26.9.17.0", {"start": v(-15.37, -28.08) * mm, "end": v(-14.77, -26.11) * mm});
            skLineSegment(sketch, "E26.2.18.0", {"start": v(-9, -30.73) * mm, "end": v(-8.03, -28.9) * mm});
            skLineSegment(sketch, "E26.3.18.0", {"start": v(-9.89, -30.43) * mm, "end": v(-9, -30.73) * mm});
            skLineSegment(sketch, "E26.6.18.0", {"start": v(-9.89, -30.43) * mm, "end": v(-10.78, -30.14) * mm});
            skLineSegment(sketch, "E26.9.18.0", {"start": v(-10.78, -30.14) * mm, "end": v(-10.5, -28.1) * mm});
            skLineSegment(sketch, "E26.2.19.0", {"start": v(-4.08, -31.75) * mm, "end": v(-3.4, -29.8) * mm});
            skLineSegment(sketch, "E26.3.19.0", {"start": v(-5, -31.6) * mm, "end": v(-4.08, -31.75) * mm});
            skLineSegment(sketch, "E26.6.19.0", {"start": v(-5, -31.6) * mm, "end": v(-5.94, -31.46) * mm});
            skLineSegment(sketch, "E26.9.19.0", {"start": v(-5.94, -31.46) * mm, "end": v(-5.97, -29.4) * mm});
            skLineSegment(sketch, "E26.2.20.0", {"start": v(0.94, -32) * mm, "end": v(1.3, -29.97) * mm});
            skLineSegment(sketch, "E26.3.20.0", {"start": v(0, -32) * mm, "end": v(0.94, -32) * mm});
            skLineSegment(sketch, "E26.6.20.0", {"start": v(0, -32) * mm, "end": v(-0.94, -32) * mm});
            skLineSegment(sketch, "E26.9.20.0", {"start": v(-0.94, -32) * mm, "end": v(-1.3, -29.97) * mm});
            skLineSegment(sketch, "E26.2.21.0", {"start": v(5.94, -31.46) * mm, "end": v(5.97, -29.4) * mm});
            skLineSegment(sketch, "E26.3.21.0", {"start": v(5, -31.6) * mm, "end": v(5.94, -31.46) * mm});
            skLineSegment(sketch, "E26.6.21.0", {"start": v(5, -31.6) * mm, "end": v(4.08, -31.75) * mm});
            skLineSegment(sketch, "E26.9.21.0", {"start": v(4.08, -31.75) * mm, "end": v(3.4, -29.8) * mm});
            skLineSegment(sketch, "E26.2.22.0", {"start": v(10.78, -30.14) * mm, "end": v(10.5, -28.1) * mm});
            skLineSegment(sketch, "E26.3.22.0", {"start": v(9.89, -30.43) * mm, "end": v(10.78, -30.14) * mm});
            skLineSegment(sketch, "E26.6.22.0", {"start": v(9.89, -30.43) * mm, "end": v(9, -30.73) * mm});
            skLineSegment(sketch, "E26.9.22.0", {"start": v(9, -30.73) * mm, "end": v(8.03, -28.9) * mm});
            skLineSegment(sketch, "E26.2.23.0", {"start": v(15.37, -28.08) * mm, "end": v(14.77, -26.11) * mm});
            skLineSegment(sketch, "E26.3.23.0", {"start": v(14.53, -28.51) * mm, "end": v(15.37, -28.08) * mm});
            skLineSegment(sketch, "E26.6.23.0", {"start": v(14.53, -28.51) * mm, "end": v(13.69, -28.94) * mm});
            skLineSegment(sketch, "E26.9.23.0", {"start": v(13.69, -28.94) * mm, "end": v(12.45, -27.3) * mm});
            skLineSegment(sketch, "E26.2.24.0", {"start": v(19.57, -25.33) * mm, "end": v(18.67, -23.48) * mm});
            skLineSegment(sketch, "E26.3.24.0", {"start": v(18.8, -25.89) * mm, "end": v(19.57, -25.33) * mm});
            skLineSegment(sketch, "E26.6.24.0", {"start": v(18.8, -25.89) * mm, "end": v(18.05, -26.44) * mm});
            skLineSegment(sketch, "E26.9.24.0", {"start": v(18.05, -26.44) * mm, "end": v(16.57, -25.01) * mm});
            skLineSegment(sketch, "E26.2.25.0", {"start": v(23.3, -21.96) * mm, "end": v(22.11, -20.27) * mm});
            skLineSegment(sketch, "E26.3.25.0", {"start": v(22.63, -22.63) * mm, "end": v(23.3, -21.96) * mm});
            skLineSegment(sketch, "E26.6.25.0", {"start": v(22.63, -22.63) * mm, "end": v(21.96, -23.3) * mm});
            skLineSegment(sketch, "E26.9.25.0", {"start": v(21.96, -23.3) * mm, "end": v(20.27, -22.11) * mm});
            skLineSegment(sketch, "E26.2.26.0", {"start": v(26.44, -18.05) * mm, "end": v(25.01, -16.57) * mm});
            skLineSegment(sketch, "E26.3.26.0", {"start": v(25.89, -18.8) * mm, "end": v(26.44, -18.05) * mm});
            skLineSegment(sketch, "E26.6.26.0", {"start": v(25.89, -18.8) * mm, "end": v(25.33, -19.57) * mm});
            skLineSegment(sketch, "E26.9.26.0", {"start": v(25.33, -19.57) * mm, "end": v(23.48, -18.67) * mm});
            skLineSegment(sketch, "E26.2.27.0", {"start": v(28.94, -13.69) * mm, "end": v(27.3, -12.45) * mm});
            skLineSegment(sketch, "E26.3.27.0", {"start": v(28.51, -14.53) * mm, "end": v(28.94, -13.69) * mm});
            skLineSegment(sketch, "E26.6.27.0", {"start": v(28.51, -14.53) * mm, "end": v(28.08, -15.37) * mm});
            skLineSegment(sketch, "E26.9.27.0", {"start": v(28.08, -15.37) * mm, "end": v(26.11, -14.77) * mm});
            skLineSegment(sketch, "E26.2.28.0", {"start": v(30.73, -9) * mm, "end": v(28.9, -8.03) * mm});
            skLineSegment(sketch, "E26.3.28.0", {"start": v(30.43, -9.89) * mm, "end": v(30.73, -9) * mm});
            skLineSegment(sketch, "E26.6.28.0", {"start": v(30.43, -9.89) * mm, "end": v(30.14, -10.78) * mm});
            skLineSegment(sketch, "E26.9.28.0", {"start": v(30.14, -10.78) * mm, "end": v(28.1, -10.5) * mm});
            skLineSegment(sketch, "E26.2.29.0", {"start": v(31.75, -4.08) * mm, "end": v(29.8, -3.4) * mm});
            skLineSegment(sketch, "E26.3.29.0", {"start": v(31.6, -5) * mm, "end": v(31.75, -4.08) * mm});
            skLineSegment(sketch, "E26.6.29.0", {"start": v(31.6, -5) * mm, "end": v(31.46, -5.94) * mm});
            skLineSegment(sketch, "E26.9.29.0", {"start": v(31.46, -5.94) * mm, "end": v(29.4, -5.97) * mm});
            skLineSegment(sketch, "E26.2.30.0", {"start": v(32, 0.94) * mm, "end": v(29.97, 1.3) * mm});
            skLineSegment(sketch, "E26.3.30.0", {"start": v(32, 0) * mm, "end": v(32, 0.94) * mm});
            skLineSegment(sketch, "E26.6.30.0", {"start": v(32, 0) * mm, "end": v(32, -0.94) * mm});
            skLineSegment(sketch, "E26.9.30.0", {"start": v(32, -0.94) * mm, "end": v(29.97, -1.3) * mm});
            skLineSegment(sketch, "E26.2.31.0", {"start": v(31.46, 5.94) * mm, "end": v(29.4, 5.97) * mm});
            skLineSegment(sketch, "E26.3.31.0", {"start": v(31.6, 5) * mm, "end": v(31.46, 5.94) * mm});
            skLineSegment(sketch, "E26.6.31.0", {"start": v(31.6, 5) * mm, "end": v(31.75, 4.08) * mm});
            skLineSegment(sketch, "E26.9.31.0", {"start": v(31.75, 4.08) * mm, "end": v(29.8, 3.4) * mm});
            skLineSegment(sketch, "E26.2.32.0", {"start": v(30.14, 10.78) * mm, "end": v(28.1, 10.5) * mm});
            skLineSegment(sketch, "E26.3.32.0", {"start": v(30.43, 9.89) * mm, "end": v(30.14, 10.78) * mm});
            skLineSegment(sketch, "E26.6.32.0", {"start": v(30.43, 9.89) * mm, "end": v(30.73, 9) * mm});
            skLineSegment(sketch, "E26.9.32.0", {"start": v(30.73, 9) * mm, "end": v(28.9, 8.03) * mm});
            skLineSegment(sketch, "E26.2.33.0", {"start": v(28.08, 15.37) * mm, "end": v(26.11, 14.77) * mm});
            skLineSegment(sketch, "E26.3.33.0", {"start": v(28.51, 14.53) * mm, "end": v(28.08, 15.37) * mm});
            skLineSegment(sketch, "E26.6.33.0", {"start": v(28.51, 14.53) * mm, "end": v(28.94, 13.69) * mm});
            skLineSegment(sketch, "E26.9.33.0", {"start": v(28.94, 13.69) * mm, "end": v(27.3, 12.45) * mm});
            skLineSegment(sketch, "E26.2.34.0", {"start": v(25.33, 19.57) * mm, "end": v(23.48, 18.67) * mm});
            skLineSegment(sketch, "E26.3.34.0", {"start": v(25.89, 18.8) * mm, "end": v(25.33, 19.57) * mm});
            skLineSegment(sketch, "E26.6.34.0", {"start": v(25.89, 18.8) * mm, "end": v(26.44, 18.05) * mm});
            skLineSegment(sketch, "E26.9.34.0", {"start": v(26.44, 18.05) * mm, "end": v(25.01, 16.57) * mm});
            skLineSegment(sketch, "E26.2.35.0", {"start": v(21.96, 23.3) * mm, "end": v(20.27, 22.11) * mm});
            skLineSegment(sketch, "E26.3.35.0", {"start": v(22.63, 22.63) * mm, "end": v(21.96, 23.3) * mm});
            skLineSegment(sketch, "E26.6.35.0", {"start": v(22.63, 22.63) * mm, "end": v(23.3, 21.96) * mm});
            skLineSegment(sketch, "E26.9.35.0", {"start": v(23.3, 21.96) * mm, "end": v(22.11, 20.27) * mm});
            skLineSegment(sketch, "E26.2.36.0", {"start": v(18.05, 26.44) * mm, "end": v(16.57, 25.01) * mm});
            skLineSegment(sketch, "E26.3.36.0", {"start": v(18.8, 25.89) * mm, "end": v(18.05, 26.44) * mm});
            skLineSegment(sketch, "E26.6.36.0", {"start": v(18.8, 25.89) * mm, "end": v(19.57, 25.33) * mm});
            skLineSegment(sketch, "E26.9.36.0", {"start": v(19.57, 25.33) * mm, "end": v(18.67, 23.48) * mm});
            skLineSegment(sketch, "E26.2.37.0", {"start": v(13.69, 28.94) * mm, "end": v(12.45, 27.3) * mm});
            skLineSegment(sketch, "E26.3.37.0", {"start": v(14.53, 28.51) * mm, "end": v(13.69, 28.94) * mm});
            skLineSegment(sketch, "E26.6.37.0", {"start": v(14.53, 28.51) * mm, "end": v(15.37, 28.08) * mm});
            skLineSegment(sketch, "E26.9.37.0", {"start": v(15.37, 28.08) * mm, "end": v(14.77, 26.11) * mm});
            skLineSegment(sketch, "E26.2.38.0", {"start": v(9, 30.73) * mm, "end": v(8.03, 28.9) * mm});
            skLineSegment(sketch, "E26.3.38.0", {"start": v(9.89, 30.43) * mm, "end": v(9, 30.73) * mm});
            skLineSegment(sketch, "E26.6.38.0", {"start": v(9.89, 30.43) * mm, "end": v(10.78, 30.14) * mm});
            skLineSegment(sketch, "E26.9.38.0", {"start": v(10.78, 30.14) * mm, "end": v(10.5, 28.1) * mm});
            skLineSegment(sketch, "E26.2.39.0", {"start": v(4.08, 31.75) * mm, "end": v(3.4, 29.8) * mm});
            skLineSegment(sketch, "E26.3.39.0", {"start": v(5, 31.6) * mm, "end": v(4.08, 31.75) * mm});
            skLineSegment(sketch, "E26.6.39.0", {"start": v(5, 31.6) * mm, "end": v(5.94, 31.46) * mm});
            skLineSegment(sketch, "E26.9.39.0", {"start": v(5.94, 31.46) * mm, "end": v(5.97, 29.4) * mm});
            skCircle(sketch, "E27.0", {"center": v(0, 0) * mm, "radius": 3 * mm});
            skSolve(sketch);
        }
        {
            var Q0;
            Q0 = qSketchRegion(id + "F14", true);
            extrude(context, id + "F15", {"entities" : qUnion([Q0]), "operationType" : NewBodyOperationType.ADD, "depth" : 4 * mm, "offsetDistance" : 25 * mm});
        }
        {
            var Q0;
            Q0=makeQuery(id+"F7.opExtrude","CAP_FACE",FACE,{"disambiguationData":[OSD([sQuery(id+"F0.wireOp",EDGE,"E0")])],"isStart":false});
            var sketch = newSketch(context, id + "F16", { "sketchPlane" : qUnion([Q0])});
            skCircle(sketch, "E28", {"center": v(40, 0) * mm, "radius": 7.5 * mm});
            skLineSegment(sketch, "E29", {"start": v(40, 0) * mm, "end": v(40, 7.5) * mm, "construction": true});
            skLineSegment(sketch, "E30", {"start": v(38.68, 7.38) * mm, "end": v(39.06, 9.5) * mm});
            skLineSegment(sketch, "E31", {"start": v(39.06, 9.5) * mm, "end": v(40.94, 9.5) * mm});
            skLineSegment(sketch, "E32.MirrorCS", {"start": v(41.32, 7.38) * mm, "end": v(40.94, 9.5) * mm});
            skLineSegment(sketch, "E33.1.0", {"start": v(34.6, 5.2) * mm, "end": v(33.65, 7.13) * mm});
            skLineSegment(sketch, "E33.1.1", {"start": v(33.65, 7.13) * mm, "end": v(35.18, 8.24) * mm});
            skLineSegment(sketch, "E33.1.2", {"start": v(36.72, 6.75) * mm, "end": v(35.18, 8.24) * mm});
            skLineSegment(sketch, "E33.2.0", {"start": v(32.57, 1.03) * mm, "end": v(30.67, 2.04) * mm});
            skLineSegment(sketch, "E33.2.1", {"start": v(30.67, 2.04) * mm, "end": v(31.26, 3.83) * mm});
            skLineSegment(sketch, "E33.2.2", {"start": v(33.38, 3.53) * mm, "end": v(31.26, 3.83) * mm});
            skLineSegment(sketch, "E34.1.3.0", {"start": v(33.38, -3.53) * mm, "end": v(31.26, -3.83) * mm});
            skLineSegment(sketch, "E34.3.3.0", {"start": v(31.26, -3.83) * mm, "end": v(30.67, -2.04) * mm});
            skLineSegment(sketch, "E34.6.3.0", {"start": v(32.57, -1.03) * mm, "end": v(30.67, -2.04) * mm});
            skLineSegment(sketch, "E34.1.4.0", {"start": v(36.72, -6.75) * mm, "end": v(35.18, -8.24) * mm});
            skLineSegment(sketch, "E34.3.4.0", {"start": v(35.18, -8.24) * mm, "end": v(33.65, -7.13) * mm});
            skLineSegment(sketch, "E34.6.4.0", {"start": v(34.6, -5.2) * mm, "end": v(33.65, -7.13) * mm});
            skLineSegment(sketch, "E34.1.5.0", {"start": v(41.32, -7.38) * mm, "end": v(40.94, -9.5) * mm});
            skLineSegment(sketch, "E34.3.5.0", {"start": v(40.94, -9.5) * mm, "end": v(39.06, -9.5) * mm});
            skLineSegment(sketch, "E34.6.5.0", {"start": v(38.68, -7.38) * mm, "end": v(39.06, -9.5) * mm});
            skLineSegment(sketch, "E34.1.6.0", {"start": v(45.4, -5.2) * mm, "end": v(46.35, -7.13) * mm});
            skLineSegment(sketch, "E34.3.6.0", {"start": v(46.35, -7.13) * mm, "end": v(44.82, -8.24) * mm});
            skLineSegment(sketch, "E34.6.6.0", {"start": v(43.28, -6.75) * mm, "end": v(44.82, -8.24) * mm});
            skLineSegment(sketch, "E34.1.7.0", {"start": v(47.43, -1.03) * mm, "end": v(49.33, -2.04) * mm});
            skLineSegment(sketch, "E34.3.7.0", {"start": v(49.33, -2.04) * mm, "end": v(48.74, -3.83) * mm});
            skLineSegment(sketch, "E34.6.7.0", {"start": v(46.62, -3.53) * mm, "end": v(48.74, -3.83) * mm});
            skLineSegment(sketch, "E34.1.8.0", {"start": v(46.62, 3.53) * mm, "end": v(48.74, 3.83) * mm});
            skLineSegment(sketch, "E34.3.8.0", {"start": v(48.74, 3.83) * mm, "end": v(49.33, 2.04) * mm});
            skLineSegment(sketch, "E34.6.8.0", {"start": v(47.43, 1.03) * mm, "end": v(49.33, 2.04) * mm});
            skLineSegment(sketch, "E34.1.9.0", {"start": v(43.28, 6.75) * mm, "end": v(44.82, 8.24) * mm});
            skLineSegment(sketch, "E34.3.9.0", {"start": v(44.82, 8.24) * mm, "end": v(46.35, 7.13) * mm});
            skLineSegment(sketch, "E34.6.9.0", {"start": v(45.4, 5.2) * mm, "end": v(46.35, 7.13) * mm});
            skSolve(sketch);
        }
        {
            var Q0;
            Q0 = qSketchRegion(id + "F16", true);
            extrude(context, id + "F17", {"entities" : qUnion([Q0]), "operationType" : NewBodyOperationType.ADD, "depth" : 4 * mm, "offsetDistance" : 25 * mm});
        }
        {
            var Q0;
            Q0=makeQuery(id+"F17.opExtrude","CAP_FACE",FACE,{"disambiguationData":[OSD([sQuery(id+"F16.wireOp",EDGE,"E28"),sQuery(id+"F16.wireOp",EDGE,"E30"),sQuery(id+"F16.wireOp",EDGE,"E31"),sQuery(id+"F16.wireOp",EDGE,"E32.MirrorCS"),sQuery(id+"F16.wireOp",EDGE,"E33.1.0"),sQuery(id+"F16.wireOp",EDGE,"E33.1.1"),sQuery(id+"F16.wireOp",EDGE,"E33.1.2"),sQuery(id+"F16.wireOp",EDGE,"E33.2.0"),sQuery(id+"F16.wireOp",EDGE,"E33.2.1"),sQuery(id+"F16.wireOp",EDGE,"E33.2.2"),sQuery(id+"F16.wireOp",EDGE,"E34.1.3.0"),sQuery(id+"F16.wireOp",EDGE,"E34.3.3.0"),sQuery(id+"F16.wireOp",EDGE,"E34.6.3.0"),sQuery(id+"F16.wireOp",EDGE,"E34.1.4.0"),sQuery(id+"F16.wireOp",EDGE,"E34.3.4.0"),sQuery(id+"F16.wireOp",EDGE,"E34.6.4.0"),sQuery(id+"F16.wireOp",EDGE,"E34.1.5.0"),sQuery(id+"F16.wireOp",EDGE,"E34.3.5.0"),sQuery(id+"F16.wireOp",EDGE,"E34.6.5.0"),sQuery(id+"F16.wireOp",EDGE,"E34.1.6.0"),sQuery(id+"F16.wireOp",EDGE,"E34.3.6.0"),sQuery(id+"F16.wireOp",EDGE,"E34.6.6.0"),sQuery(id+"F16.wireOp",EDGE,"E34.1.7.0"),sQuery(id+"F16.wireOp",EDGE,"E34.3.7.0"),sQuery(id+"F16.wireOp",EDGE,"E34.6.7.0"),sQuery(id+"F16.wireOp",EDGE,"E34.1.8.0"),sQuery(id+"F16.wireOp",EDGE,"E34.3.8.0"),sQuery(id+"F16.wireOp",EDGE,"E34.6.8.0"),sQuery(id+"F16.wireOp",EDGE,"E34.1.9.0"),sQuery(id+"F16.wireOp",EDGE,"E34.3.9.0"),sQuery(id+"F16.wireOp",EDGE,"E34.6.9.0")])],"isStart":false});
            var sketch = newSketch(context, id + "F18", { "sketchPlane" : qUnion([Q0])});
            skCircle(sketch, "E35.0", {"center": v(40, 0) * mm, "radius": 3 * mm});
            skSolve(sketch);
        }
        {
            var Q0;
            Q0 = qSketchRegion(id + "F18", true);
            extrude(context, id + "F19", {"entities" : qUnion([Q0]), "operationType" : NewBodyOperationType.ADD, "depth" : 2 * mm, "offsetDistance" : 25 * mm});
        }
        {
            var Q0;
            Q0=makeQuery(id+"F19.opExtrude","CAP_FACE",FACE,{"disambiguationData":[OSD([sQuery(id+"F18.wireOp",EDGE,"E35.0")])],"isStart":false});
            var sketch = newSketch(context, id + "F20", { "sketchPlane" : qUnion([Q0])});
            skCircle(sketch, "E36", {"center": v(0, 0) * mm, "radius": 94 * mm});
            skCircle(sketch, "E37.0", {"center": v(0, 0) * mm, "radius": 5 * mm});
            skSolve(sketch);
        }
        {
            var Q0;
            Q0 = qSketchRegion(id + "F20", true);
            extrude(context, id + "F21", {"entities" : qUnion([Q0]), "depth" : 1 * mm, "offsetDistance" : 25 * mm});
        }
        {
            var Q0;
            Q0=makeQuery(id+"F21.opExtrude","SWEPT_BODY",BODY,{"disambiguationData":[OSD([sQuery(id+"F20.wireOp",EDGE,"E36"),sQuery(id+"F20.wireOp",EDGE,"E37.0")])]});
            var Q1;
            Q1=makeQuery(id+"F1.opExtrude","SWEPT_BODY",BODY,{"disambiguationData":[OSD([sQuery(id+"F0.wireOp",EDGE,"E0")])]});
            booleanBodies(context, id + "F22", {"operationType" : BooleanOperationType.SUBTRACTION, "tools" : qUnion([Q0]), "targets" : qUnion([Q1]), "keepTools" : true});
        }
        {
            var Q0;
            Q0=makeQuery(id+"F21.opExtrude","CAP_FACE",FACE,{"disambiguationData":[OSD([sQuery(id+"F20.wireOp",EDGE,"E36"),sQuery(id+"F20.wireOp",EDGE,"E37.0")])],"isStart":true});
            var sketch = newSketch(context, id + "F23", { "sketchPlane" : qUnion([Q0])});
            skCircle(sketch, "E38.0.0", {"center": v(-40, 0) * mm, "radius": 3 * mm});
            skCircle(sketch, "E39.0.0", {"center": v(0, 0) * mm, "radius": 90 * mm});
            skCircle(sketch, "E40", {"center": v(-40, 0) * mm, "radius": 5 * mm});
            skSolve(sketch);
        }
        {
            var Q0;
            Q0 = qSketchRegion(id + "F23", true);
            var Q1;
            Q1 = qSketchRegion(id + "F25", true);
            extrude(context, id + "F24", {"entities" : qUnion([Q0, Q1]), "operationType" : NewBodyOperationType.ADD, "endBound" : BoundingType.UP_TO_NEXT, "depth" : 25 * mm, "offsetDistance" : 25 * mm});
        }
        {
            var Q0;
            Q0=makeQuery(id+"F21.opExtrude","CAP_FACE",FACE,{"disambiguationData":[OSD([sQuery(id+"F20.wireOp",EDGE,"E36"),sQuery(id+"F20.wireOp",EDGE,"E37.0")])],"isStart":false});
            var sketch = newSketch(context, id + "F25", { "sketchPlane" : qUnion([Q0])});
            skLineSegment(sketch, "E41.bottom", {"start": v(-1.5, 88.99) * mm, "end": v(1.5, 88.99) * mm});
            skLineSegment(sketch, "E41.top", {"start": v(-1.5, 68.99) * mm, "end": v(1.5, 68.99) * mm});
            skLineSegment(sketch, "E41.left", {"start": v(-1.5, 88.99) * mm, "end": v(-1.5, 68.99) * mm});
            skLineSegment(sketch, "E41.right", {"start": v(1.5, 88.99) * mm, "end": v(1.5, 68.99) * mm});
            skPoint(sketch, "E41.middle", {"position": v(0, 78.99) * mm});
            skLineSegment(sketch, "E42.1.0", {"start": v(-45.8, 76.32) * mm, "end": v(-43.2, 77.82) * mm});
            skLineSegment(sketch, "E42.1.1", {"start": v(-43.2, 77.82) * mm, "end": v(-33.2, 60.5) * mm});
            skLineSegment(sketch, "E42.1.2", {"start": v(-35.8, 59) * mm, "end": v(-33.2, 60.5) * mm});
            skLineSegment(sketch, "E42.1.3", {"start": v(-45.8, 76.32) * mm, "end": v(-35.8, 59) * mm});
            skLineSegment(sketch, "E42.2.0", {"start": v(-77.82, 43.2) * mm, "end": v(-76.32, 45.8) * mm});
            skLineSegment(sketch, "E42.2.1", {"start": v(-76.32, 45.8) * mm, "end": v(-59, 35.8) * mm});
            skLineSegment(sketch, "E42.2.2", {"start": v(-60.5, 33.2) * mm, "end": v(-59, 35.8) * mm});
            skLineSegment(sketch, "E42.2.3", {"start": v(-77.82, 43.2) * mm, "end": v(-60.5, 33.2) * mm});
            skPoint(sketch, "E42.center", {"position": v(0, 0) * mm});
            skLineSegment(sketch, "E43.1.3.0", {"start": v(-88.99, -1.5) * mm, "end": v(-88.99, 1.5) * mm});
            skLineSegment(sketch, "E43.3.3.0", {"start": v(-88.99, 1.5) * mm, "end": v(-68.99, 1.5) * mm});
            skLineSegment(sketch, "E43.6.3.0", {"start": v(-68.99, -1.5) * mm, "end": v(-68.99, 1.5) * mm});
            skLineSegment(sketch, "E43.9.3.0", {"start": v(-88.99, -1.5) * mm, "end": v(-68.99, -1.5) * mm});
            skLineSegment(sketch, "E43.1.4.0", {"start": v(-76.32, -45.8) * mm, "end": v(-77.82, -43.2) * mm});
            skLineSegment(sketch, "E43.3.4.0", {"start": v(-77.82, -43.2) * mm, "end": v(-60.5, -33.2) * mm});
            skLineSegment(sketch, "E43.6.4.0", {"start": v(-59, -35.8) * mm, "end": v(-60.5, -33.2) * mm});
            skLineSegment(sketch, "E43.9.4.0", {"start": v(-76.32, -45.8) * mm, "end": v(-59, -35.8) * mm});
            skLineSegment(sketch, "E43.1.5.0", {"start": v(-43.2, -77.82) * mm, "end": v(-45.8, -76.32) * mm});
            skLineSegment(sketch, "E43.3.5.0", {"start": v(-45.8, -76.32) * mm, "end": v(-35.8, -59) * mm});
            skLineSegment(sketch, "E43.6.5.0", {"start": v(-33.2, -60.5) * mm, "end": v(-35.8, -59) * mm});
            skLineSegment(sketch, "E43.9.5.0", {"start": v(-43.2, -77.82) * mm, "end": v(-33.2, -60.5) * mm});
            skLineSegment(sketch, "E43.1.6.0", {"start": v(1.5, -88.99) * mm, "end": v(-1.5, -88.99) * mm});
            skLineSegment(sketch, "E43.3.6.0", {"start": v(-1.5, -88.99) * mm, "end": v(-1.5, -68.99) * mm});
            skLineSegment(sketch, "E43.6.6.0", {"start": v(1.5, -68.99) * mm, "end": v(-1.5, -68.99) * mm});
            skLineSegment(sketch, "E43.9.6.0", {"start": v(1.5, -88.99) * mm, "end": v(1.5, -68.99) * mm});
            skLineSegment(sketch, "E43.1.7.0", {"start": v(45.8, -76.32) * mm, "end": v(43.2, -77.82) * mm});
            skLineSegment(sketch, "E43.3.7.0", {"start": v(43.2, -77.82) * mm, "end": v(33.2, -60.5) * mm});
            skLineSegment(sketch, "E43.6.7.0", {"start": v(35.8, -59) * mm, "end": v(33.2, -60.5) * mm});
            skLineSegment(sketch, "E43.9.7.0", {"start": v(45.8, -76.32) * mm, "end": v(35.8, -59) * mm});
            skLineSegment(sketch, "E43.1.8.0", {"start": v(77.82, -43.2) * mm, "end": v(76.32, -45.8) * mm});
            skLineSegment(sketch, "E43.3.8.0", {"start": v(76.32, -45.8) * mm, "end": v(59, -35.8) * mm});
            skLineSegment(sketch, "E43.6.8.0", {"start": v(60.5, -33.2) * mm, "end": v(59, -35.8) * mm});
            skLineSegment(sketch, "E43.9.8.0", {"start": v(77.82, -43.2) * mm, "end": v(60.5, -33.2) * mm});
            skLineSegment(sketch, "E43.1.9.0", {"start": v(88.99, 1.5) * mm, "end": v(88.99, -1.5) * mm});
            skLineSegment(sketch, "E43.3.9.0", {"start": v(88.99, -1.5) * mm, "end": v(68.99, -1.5) * mm});
            skLineSegment(sketch, "E43.6.9.0", {"start": v(68.99, 1.5) * mm, "end": v(68.99, -1.5) * mm});
            skLineSegment(sketch, "E43.9.9.0", {"start": v(88.99, 1.5) * mm, "end": v(68.99, 1.5) * mm});
            skLineSegment(sketch, "E43.1.10.0", {"start": v(76.32, 45.8) * mm, "end": v(77.82, 43.2) * mm});
            skLineSegment(sketch, "E43.3.10.0", {"start": v(77.82, 43.2) * mm, "end": v(60.5, 33.2) * mm});
            skLineSegment(sketch, "E43.6.10.0", {"start": v(59, 35.8) * mm, "end": v(60.5, 33.2) * mm});
            skLineSegment(sketch, "E43.9.10.0", {"start": v(76.32, 45.8) * mm, "end": v(59, 35.8) * mm});
            skLineSegment(sketch, "E43.1.11.0", {"start": v(43.2, 77.82) * mm, "end": v(45.8, 76.32) * mm});
            skLineSegment(sketch, "E43.3.11.0", {"start": v(45.8, 76.32) * mm, "end": v(35.8, 59) * mm});
            skLineSegment(sketch, "E43.6.11.0", {"start": v(33.2, 60.5) * mm, "end": v(35.8, 59) * mm});
            skLineSegment(sketch, "E43.9.11.0", {"start": v(43.2, 77.82) * mm, "end": v(33.2, 60.5) * mm});
            skSolve(sketch);
        }
        {
            var Q0;
            Q0 = qSketchRegion(id + "F25", true);
            extrude(context, id + "F26", {"entities" : qUnion([Q0]), "operationType" : NewBodyOperationType.REMOVE, "oppositeDirection" : true, "depth" : 0.5 * mm, "offsetDistance" : 25 * mm});
        }
        {
            var Q0;
            Q0=makeQuery(id+"F21.opExtrude","CAP_FACE",FACE,{"disambiguationData":[OSD([sQuery(id+"F20.wireOp",EDGE,"E36"),sQuery(id+"F20.wireOp",EDGE,"E37.0")])],"isStart":false});
            var sketch = newSketch(context, id + "F27", { "sketchPlane" : qUnion([Q0])});
            skLineSegment(sketch, "E44.bottom", {"start": v(-0.75, 88.49) * mm, "end": v(0.75, 88.49) * mm});
            skLineSegment(sketch, "E44.top", {"start": v(-0.75, 76.49) * mm, "end": v(0.75, 76.49) * mm});
            skLineSegment(sketch, "E44.left", {"start": v(-0.75, 88.49) * mm, "end": v(-0.75, 76.49) * mm});
            skLineSegment(sketch, "E44.right", {"start": v(0.75, 88.49) * mm, "end": v(0.75, 76.49) * mm});
            skPoint(sketch, "E44.middle", {"position": v(0, 82.49) * mm});
            skLineSegment(sketch, "E45.1.0", {"start": v(-8.74, 75.99) * mm, "end": v(-7.25, 76.15) * mm});
            skLineSegment(sketch, "E45.1.1", {"start": v(-8.5, 88.08) * mm, "end": v(-7.25, 76.15) * mm});
            skLineSegment(sketch, "E45.1.2", {"start": v(-10, 87.92) * mm, "end": v(-8.74, 75.99) * mm});
            skLineSegment(sketch, "E45.1.3", {"start": v(-10, 87.92) * mm, "end": v(-8.5, 88.08) * mm});
            skLineSegment(sketch, "E45.2.0", {"start": v(-16.64, 74.66) * mm, "end": v(-15.17, 74.97) * mm});
            skLineSegment(sketch, "E45.2.1", {"start": v(-17.66, 86.7) * mm, "end": v(-15.17, 74.97) * mm});
            skLineSegment(sketch, "E45.2.2", {"start": v(-19.13, 86.4) * mm, "end": v(-16.64, 74.66) * mm});
            skLineSegment(sketch, "E45.2.3", {"start": v(-19.13, 86.4) * mm, "end": v(-17.66, 86.7) * mm});
            skPoint(sketch, "E45.center", {"position": v(0, 0) * mm});
            skLineSegment(sketch, "E46.1.3.0", {"start": v(-24.35, 72.51) * mm, "end": v(-22.92, 72.98) * mm});
            skLineSegment(sketch, "E46.3.3.0", {"start": v(-26.63, 84.39) * mm, "end": v(-22.92, 72.98) * mm});
            skLineSegment(sketch, "E46.6.3.0", {"start": v(-28.06, 83.92) * mm, "end": v(-24.35, 72.51) * mm});
            skLineSegment(sketch, "E46.9.3.0", {"start": v(-28.06, 83.92) * mm, "end": v(-26.63, 84.39) * mm});
            skLineSegment(sketch, "E46.1.4.0", {"start": v(-31.8, 69.57) * mm, "end": v(-30.43, 70.18) * mm});
            skLineSegment(sketch, "E46.3.4.0", {"start": v(-35.3, 81.14) * mm, "end": v(-30.43, 70.18) * mm});
            skLineSegment(sketch, "E46.6.4.0", {"start": v(-36.68, 80.53) * mm, "end": v(-31.8, 69.57) * mm});
            skLineSegment(sketch, "E46.9.4.0", {"start": v(-36.68, 80.53) * mm, "end": v(-35.3, 81.14) * mm});
            skLineSegment(sketch, "E46.1.5.0", {"start": v(-38.9, 65.86) * mm, "end": v(-37.6, 66.61) * mm});
            skLineSegment(sketch, "E46.3.5.0", {"start": v(-43.6, 77) * mm, "end": v(-37.6, 66.61) * mm});
            skLineSegment(sketch, "E46.6.5.0", {"start": v(-44.9, 76.26) * mm, "end": v(-38.9, 65.86) * mm});
            skLineSegment(sketch, "E46.9.5.0", {"start": v(-44.9, 76.26) * mm, "end": v(-43.6, 77) * mm});
            skLineSegment(sketch, "E46.1.6.0", {"start": v(-45.56, 61.44) * mm, "end": v(-44.35, 62.32) * mm});
            skLineSegment(sketch, "E46.3.6.0", {"start": v(-51.4, 72.03) * mm, "end": v(-44.35, 62.32) * mm});
            skLineSegment(sketch, "E46.6.6.0", {"start": v(-52.62, 71.15) * mm, "end": v(-45.56, 61.44) * mm});
            skLineSegment(sketch, "E46.9.6.0", {"start": v(-52.62, 71.15) * mm, "end": v(-51.4, 72.03) * mm});
            skLineSegment(sketch, "E46.1.7.0", {"start": v(-51.74, 56.34) * mm, "end": v(-50.62, 57.34) * mm});
            skLineSegment(sketch, "E46.3.7.0", {"start": v(-58.65, 66.26) * mm, "end": v(-50.62, 57.34) * mm});
            skLineSegment(sketch, "E46.6.7.0", {"start": v(-59.77, 65.26) * mm, "end": v(-51.74, 56.34) * mm});
            skLineSegment(sketch, "E46.9.7.0", {"start": v(-59.77, 65.26) * mm, "end": v(-58.65, 66.26) * mm});
            skLineSegment(sketch, "E46.1.8.0", {"start": v(-57.34, 50.62) * mm, "end": v(-56.34, 51.74) * mm});
            skLineSegment(sketch, "E46.3.8.0", {"start": v(-65.26, 59.77) * mm, "end": v(-56.34, 51.74) * mm});
            skLineSegment(sketch, "E46.6.8.0", {"start": v(-66.26, 58.65) * mm, "end": v(-57.34, 50.62) * mm});
            skLineSegment(sketch, "E46.9.8.0", {"start": v(-66.26, 58.65) * mm, "end": v(-65.26, 59.77) * mm});
            skLineSegment(sketch, "E46.1.9.0", {"start": v(-62.32, 44.35) * mm, "end": v(-61.44, 45.56) * mm});
            skLineSegment(sketch, "E46.3.9.0", {"start": v(-71.15, 52.62) * mm, "end": v(-61.44, 45.56) * mm});
            skLineSegment(sketch, "E46.6.9.0", {"start": v(-72.03, 51.4) * mm, "end": v(-62.32, 44.35) * mm});
            skLineSegment(sketch, "E46.9.9.0", {"start": v(-72.03, 51.4) * mm, "end": v(-71.15, 52.62) * mm});
            skLineSegment(sketch, "E46.1.10.0", {"start": v(-66.61, 37.6) * mm, "end": v(-65.86, 38.9) * mm});
            skLineSegment(sketch, "E46.3.10.0", {"start": v(-76.26, 44.9) * mm, "end": v(-65.86, 38.9) * mm});
            skLineSegment(sketch, "E46.6.10.0", {"start": v(-77, 43.6) * mm, "end": v(-66.61, 37.6) * mm});
            skLineSegment(sketch, "E46.9.10.0", {"start": v(-77, 43.6) * mm, "end": v(-76.26, 44.9) * mm});
            skLineSegment(sketch, "E46.1.11.0", {"start": v(-70.18, 30.43) * mm, "end": v(-69.57, 31.8) * mm});
            skLineSegment(sketch, "E46.3.11.0", {"start": v(-80.53, 36.68) * mm, "end": v(-69.57, 31.8) * mm});
            skLineSegment(sketch, "E46.6.11.0", {"start": v(-81.14, 35.3) * mm, "end": v(-70.18, 30.43) * mm});
            skLineSegment(sketch, "E46.9.11.0", {"start": v(-81.14, 35.3) * mm, "end": v(-80.53, 36.68) * mm});
            skLineSegment(sketch, "E47.1.12.0", {"start": v(-72.98, 22.92) * mm, "end": v(-72.51, 24.35) * mm});
            skLineSegment(sketch, "E47.3.12.0", {"start": v(-83.92, 28.06) * mm, "end": v(-72.51, 24.35) * mm});
            skLineSegment(sketch, "E47.6.12.0", {"start": v(-84.39, 26.63) * mm, "end": v(-72.98, 22.92) * mm});
            skLineSegment(sketch, "E47.9.12.0", {"start": v(-84.39, 26.63) * mm, "end": v(-83.92, 28.06) * mm});
            skLineSegment(sketch, "E47.1.13.0", {"start": v(-74.97, 15.17) * mm, "end": v(-74.66, 16.64) * mm});
            skLineSegment(sketch, "E47.3.13.0", {"start": v(-86.4, 19.13) * mm, "end": v(-74.66, 16.64) * mm});
            skLineSegment(sketch, "E47.6.13.0", {"start": v(-86.7, 17.66) * mm, "end": v(-74.97, 15.17) * mm});
            skLineSegment(sketch, "E47.9.13.0", {"start": v(-86.7, 17.66) * mm, "end": v(-86.4, 19.13) * mm});
            skLineSegment(sketch, "E47.1.14.0", {"start": v(-76.15, 7.25) * mm, "end": v(-75.99, 8.74) * mm});
            skLineSegment(sketch, "E47.3.14.0", {"start": v(-87.92, 10) * mm, "end": v(-75.99, 8.74) * mm});
            skLineSegment(sketch, "E47.6.14.0", {"start": v(-88.08, 8.5) * mm, "end": v(-76.15, 7.25) * mm});
            skLineSegment(sketch, "E47.9.14.0", {"start": v(-88.08, 8.5) * mm, "end": v(-87.92, 10) * mm});
            skLineSegment(sketch, "E47.1.15.0", {"start": v(-76.49, -0.75) * mm, "end": v(-76.49, 0.75) * mm});
            skLineSegment(sketch, "E47.3.15.0", {"start": v(-88.49, 0.75) * mm, "end": v(-76.49, 0.75) * mm});
            skLineSegment(sketch, "E47.6.15.0", {"start": v(-88.49, -0.75) * mm, "end": v(-76.49, -0.75) * mm});
            skLineSegment(sketch, "E47.9.15.0", {"start": v(-88.49, -0.75) * mm, "end": v(-88.49, 0.75) * mm});
            skLineSegment(sketch, "E47.1.16.0", {"start": v(-75.99, -8.74) * mm, "end": v(-76.15, -7.25) * mm});
            skLineSegment(sketch, "E47.3.16.0", {"start": v(-88.08, -8.5) * mm, "end": v(-76.15, -7.25) * mm});
            skLineSegment(sketch, "E47.6.16.0", {"start": v(-87.92, -10) * mm, "end": v(-75.99, -8.74) * mm});
            skLineSegment(sketch, "E47.9.16.0", {"start": v(-87.92, -10) * mm, "end": v(-88.08, -8.5) * mm});
            skLineSegment(sketch, "E47.1.17.0", {"start": v(-74.66, -16.64) * mm, "end": v(-74.97, -15.17) * mm});
            skLineSegment(sketch, "E47.3.17.0", {"start": v(-86.7, -17.66) * mm, "end": v(-74.97, -15.17) * mm});
            skLineSegment(sketch, "E47.6.17.0", {"start": v(-86.4, -19.13) * mm, "end": v(-74.66, -16.64) * mm});
            skLineSegment(sketch, "E47.9.17.0", {"start": v(-86.4, -19.13) * mm, "end": v(-86.7, -17.66) * mm});
            skLineSegment(sketch, "E47.1.18.0", {"start": v(-72.51, -24.35) * mm, "end": v(-72.98, -22.92) * mm});
            skLineSegment(sketch, "E47.3.18.0", {"start": v(-84.39, -26.63) * mm, "end": v(-72.98, -22.92) * mm});
            skLineSegment(sketch, "E47.6.18.0", {"start": v(-83.92, -28.06) * mm, "end": v(-72.51, -24.35) * mm});
            skLineSegment(sketch, "E47.9.18.0", {"start": v(-83.92, -28.06) * mm, "end": v(-84.39, -26.63) * mm});
            skLineSegment(sketch, "E47.1.19.0", {"start": v(-69.57, -31.8) * mm, "end": v(-70.18, -30.43) * mm});
            skLineSegment(sketch, "E47.3.19.0", {"start": v(-81.14, -35.3) * mm, "end": v(-70.18, -30.43) * mm});
            skLineSegment(sketch, "E47.6.19.0", {"start": v(-80.53, -36.68) * mm, "end": v(-69.57, -31.8) * mm});
            skLineSegment(sketch, "E47.9.19.0", {"start": v(-80.53, -36.68) * mm, "end": v(-81.14, -35.3) * mm});
            skLineSegment(sketch, "E47.1.20.0", {"start": v(-65.86, -38.9) * mm, "end": v(-66.61, -37.6) * mm});
            skLineSegment(sketch, "E47.3.20.0", {"start": v(-77, -43.6) * mm, "end": v(-66.61, -37.6) * mm});
            skLineSegment(sketch, "E47.6.20.0", {"start": v(-76.26, -44.9) * mm, "end": v(-65.86, -38.9) * mm});
            skLineSegment(sketch, "E47.9.20.0", {"start": v(-76.26, -44.9) * mm, "end": v(-77, -43.6) * mm});
            skLineSegment(sketch, "E47.1.21.0", {"start": v(-61.44, -45.56) * mm, "end": v(-62.32, -44.35) * mm});
            skLineSegment(sketch, "E47.3.21.0", {"start": v(-72.03, -51.4) * mm, "end": v(-62.32, -44.35) * mm});
            skLineSegment(sketch, "E47.6.21.0", {"start": v(-71.15, -52.62) * mm, "end": v(-61.44, -45.56) * mm});
            skLineSegment(sketch, "E47.9.21.0", {"start": v(-71.15, -52.62) * mm, "end": v(-72.03, -51.4) * mm});
            skLineSegment(sketch, "E47.1.22.0", {"start": v(-56.34, -51.74) * mm, "end": v(-57.34, -50.62) * mm});
            skLineSegment(sketch, "E47.3.22.0", {"start": v(-66.26, -58.65) * mm, "end": v(-57.34, -50.62) * mm});
            skLineSegment(sketch, "E47.6.22.0", {"start": v(-65.26, -59.77) * mm, "end": v(-56.34, -51.74) * mm});
            skLineSegment(sketch, "E47.9.22.0", {"start": v(-65.26, -59.77) * mm, "end": v(-66.26, -58.65) * mm});
            skLineSegment(sketch, "E47.1.23.0", {"start": v(-50.62, -57.34) * mm, "end": v(-51.74, -56.34) * mm});
            skLineSegment(sketch, "E47.3.23.0", {"start": v(-59.77, -65.26) * mm, "end": v(-51.74, -56.34) * mm});
            skLineSegment(sketch, "E47.6.23.0", {"start": v(-58.65, -66.26) * mm, "end": v(-50.62, -57.34) * mm});
            skLineSegment(sketch, "E47.9.23.0", {"start": v(-58.65, -66.26) * mm, "end": v(-59.77, -65.26) * mm});
            skLineSegment(sketch, "E47.1.24.0", {"start": v(-44.35, -62.32) * mm, "end": v(-45.56, -61.44) * mm});
            skLineSegment(sketch, "E47.3.24.0", {"start": v(-52.62, -71.15) * mm, "end": v(-45.56, -61.44) * mm});
            skLineSegment(sketch, "E47.6.24.0", {"start": v(-51.4, -72.03) * mm, "end": v(-44.35, -62.32) * mm});
            skLineSegment(sketch, "E47.9.24.0", {"start": v(-51.4, -72.03) * mm, "end": v(-52.62, -71.15) * mm});
            skLineSegment(sketch, "E47.1.25.0", {"start": v(-37.6, -66.61) * mm, "end": v(-38.9, -65.86) * mm});
            skLineSegment(sketch, "E47.3.25.0", {"start": v(-44.9, -76.26) * mm, "end": v(-38.9, -65.86) * mm});
            skLineSegment(sketch, "E47.6.25.0", {"start": v(-43.6, -77) * mm, "end": v(-37.6, -66.61) * mm});
            skLineSegment(sketch, "E47.9.25.0", {"start": v(-43.6, -77) * mm, "end": v(-44.9, -76.26) * mm});
            skLineSegment(sketch, "E47.1.26.0", {"start": v(-30.43, -70.18) * mm, "end": v(-31.8, -69.57) * mm});
            skLineSegment(sketch, "E47.3.26.0", {"start": v(-36.68, -80.53) * mm, "end": v(-31.8, -69.57) * mm});
            skLineSegment(sketch, "E47.6.26.0", {"start": v(-35.3, -81.14) * mm, "end": v(-30.43, -70.18) * mm});
            skLineSegment(sketch, "E47.9.26.0", {"start": v(-35.3, -81.14) * mm, "end": v(-36.68, -80.53) * mm});
            skLineSegment(sketch, "E47.1.27.0", {"start": v(-22.92, -72.98) * mm, "end": v(-24.35, -72.51) * mm});
            skLineSegment(sketch, "E47.3.27.0", {"start": v(-28.06, -83.92) * mm, "end": v(-24.35, -72.51) * mm});
            skLineSegment(sketch, "E47.6.27.0", {"start": v(-26.63, -84.39) * mm, "end": v(-22.92, -72.98) * mm});
            skLineSegment(sketch, "E47.9.27.0", {"start": v(-26.63, -84.39) * mm, "end": v(-28.06, -83.92) * mm});
            skLineSegment(sketch, "E47.1.28.0", {"start": v(-15.17, -74.97) * mm, "end": v(-16.64, -74.66) * mm});
            skLineSegment(sketch, "E47.3.28.0", {"start": v(-19.13, -86.4) * mm, "end": v(-16.64, -74.66) * mm});
            skLineSegment(sketch, "E47.6.28.0", {"start": v(-17.66, -86.7) * mm, "end": v(-15.17, -74.97) * mm});
            skLineSegment(sketch, "E47.9.28.0", {"start": v(-17.66, -86.7) * mm, "end": v(-19.13, -86.4) * mm});
            skLineSegment(sketch, "E47.1.29.0", {"start": v(-7.25, -76.15) * mm, "end": v(-8.74, -75.99) * mm});
            skLineSegment(sketch, "E47.3.29.0", {"start": v(-10, -87.92) * mm, "end": v(-8.74, -75.99) * mm});
            skLineSegment(sketch, "E47.6.29.0", {"start": v(-8.5, -88.08) * mm, "end": v(-7.25, -76.15) * mm});
            skLineSegment(sketch, "E47.9.29.0", {"start": v(-8.5, -88.08) * mm, "end": v(-10, -87.92) * mm});
            skLineSegment(sketch, "E47.1.30.0", {"start": v(0.75, -76.49) * mm, "end": v(-0.75, -76.49) * mm});
            skLineSegment(sketch, "E47.3.30.0", {"start": v(-0.75, -88.49) * mm, "end": v(-0.75, -76.49) * mm});
            skLineSegment(sketch, "E47.6.30.0", {"start": v(0.75, -88.49) * mm, "end": v(0.75, -76.49) * mm});
            skLineSegment(sketch, "E47.9.30.0", {"start": v(0.75, -88.49) * mm, "end": v(-0.75, -88.49) * mm});
            skLineSegment(sketch, "E47.1.31.0", {"start": v(8.74, -75.99) * mm, "end": v(7.25, -76.15) * mm});
            skLineSegment(sketch, "E47.3.31.0", {"start": v(8.5, -88.08) * mm, "end": v(7.25, -76.15) * mm});
            skLineSegment(sketch, "E47.6.31.0", {"start": v(10, -87.92) * mm, "end": v(8.74, -75.99) * mm});
            skLineSegment(sketch, "E47.9.31.0", {"start": v(10, -87.92) * mm, "end": v(8.5, -88.08) * mm});
            skLineSegment(sketch, "E47.1.32.0", {"start": v(16.64, -74.66) * mm, "end": v(15.17, -74.97) * mm});
            skLineSegment(sketch, "E47.3.32.0", {"start": v(17.66, -86.7) * mm, "end": v(15.17, -74.97) * mm});
            skLineSegment(sketch, "E47.6.32.0", {"start": v(19.13, -86.4) * mm, "end": v(16.64, -74.66) * mm});
            skLineSegment(sketch, "E47.9.32.0", {"start": v(19.13, -86.4) * mm, "end": v(17.66, -86.7) * mm});
            skLineSegment(sketch, "E47.1.33.0", {"start": v(24.35, -72.51) * mm, "end": v(22.92, -72.98) * mm});
            skLineSegment(sketch, "E47.3.33.0", {"start": v(26.63, -84.39) * mm, "end": v(22.92, -72.98) * mm});
            skLineSegment(sketch, "E47.6.33.0", {"start": v(28.06, -83.92) * mm, "end": v(24.35, -72.51) * mm});
            skLineSegment(sketch, "E47.9.33.0", {"start": v(28.06, -83.92) * mm, "end": v(26.63, -84.39) * mm});
            skLineSegment(sketch, "E47.1.34.0", {"start": v(31.8, -69.57) * mm, "end": v(30.43, -70.18) * mm});
            skLineSegment(sketch, "E47.3.34.0", {"start": v(35.3, -81.14) * mm, "end": v(30.43, -70.18) * mm});
            skLineSegment(sketch, "E47.6.34.0", {"start": v(36.68, -80.53) * mm, "end": v(31.8, -69.57) * mm});
            skLineSegment(sketch, "E47.9.34.0", {"start": v(36.68, -80.53) * mm, "end": v(35.3, -81.14) * mm});
            skLineSegment(sketch, "E47.1.35.0", {"start": v(38.9, -65.86) * mm, "end": v(37.6, -66.61) * mm});
            skLineSegment(sketch, "E47.3.35.0", {"start": v(43.6, -77) * mm, "end": v(37.6, -66.61) * mm});
            skLineSegment(sketch, "E47.6.35.0", {"start": v(44.9, -76.26) * mm, "end": v(38.9, -65.86) * mm});
            skLineSegment(sketch, "E47.9.35.0", {"start": v(44.9, -76.26) * mm, "end": v(43.6, -77) * mm});
            skLineSegment(sketch, "E47.1.36.0", {"start": v(45.56, -61.44) * mm, "end": v(44.35, -62.32) * mm});
            skLineSegment(sketch, "E47.3.36.0", {"start": v(51.4, -72.03) * mm, "end": v(44.35, -62.32) * mm});
            skLineSegment(sketch, "E47.6.36.0", {"start": v(52.62, -71.15) * mm, "end": v(45.56, -61.44) * mm});
            skLineSegment(sketch, "E47.9.36.0", {"start": v(52.62, -71.15) * mm, "end": v(51.4, -72.03) * mm});
            skLineSegment(sketch, "E47.1.37.0", {"start": v(51.74, -56.34) * mm, "end": v(50.62, -57.34) * mm});
            skLineSegment(sketch, "E47.3.37.0", {"start": v(58.65, -66.26) * mm, "end": v(50.62, -57.34) * mm});
            skLineSegment(sketch, "E47.6.37.0", {"start": v(59.77, -65.26) * mm, "end": v(51.74, -56.34) * mm});
            skLineSegment(sketch, "E47.9.37.0", {"start": v(59.77, -65.26) * mm, "end": v(58.65, -66.26) * mm});
            skLineSegment(sketch, "E47.1.38.0", {"start": v(57.34, -50.62) * mm, "end": v(56.34, -51.74) * mm});
            skLineSegment(sketch, "E47.3.38.0", {"start": v(65.26, -59.77) * mm, "end": v(56.34, -51.74) * mm});
            skLineSegment(sketch, "E47.6.38.0", {"start": v(66.26, -58.65) * mm, "end": v(57.34, -50.62) * mm});
            skLineSegment(sketch, "E47.9.38.0", {"start": v(66.26, -58.65) * mm, "end": v(65.26, -59.77) * mm});
            skLineSegment(sketch, "E47.1.39.0", {"start": v(62.32, -44.35) * mm, "end": v(61.44, -45.56) * mm});
            skLineSegment(sketch, "E47.3.39.0", {"start": v(71.15, -52.62) * mm, "end": v(61.44, -45.56) * mm});
            skLineSegment(sketch, "E47.6.39.0", {"start": v(72.03, -51.4) * mm, "end": v(62.32, -44.35) * mm});
            skLineSegment(sketch, "E47.9.39.0", {"start": v(72.03, -51.4) * mm, "end": v(71.15, -52.62) * mm});
            skLineSegment(sketch, "E47.1.40.0", {"start": v(66.61, -37.6) * mm, "end": v(65.86, -38.9) * mm});
            skLineSegment(sketch, "E47.3.40.0", {"start": v(76.26, -44.9) * mm, "end": v(65.86, -38.9) * mm});
            skLineSegment(sketch, "E47.6.40.0", {"start": v(77, -43.6) * mm, "end": v(66.61, -37.6) * mm});
            skLineSegment(sketch, "E47.9.40.0", {"start": v(77, -43.6) * mm, "end": v(76.26, -44.9) * mm});
            skLineSegment(sketch, "E47.1.41.0", {"start": v(70.18, -30.43) * mm, "end": v(69.57, -31.8) * mm});
            skLineSegment(sketch, "E47.3.41.0", {"start": v(80.53, -36.68) * mm, "end": v(69.57, -31.8) * mm});
            skLineSegment(sketch, "E47.6.41.0", {"start": v(81.14, -35.3) * mm, "end": v(70.18, -30.43) * mm});
            skLineSegment(sketch, "E47.9.41.0", {"start": v(81.14, -35.3) * mm, "end": v(80.53, -36.68) * mm});
            skLineSegment(sketch, "E47.1.42.0", {"start": v(72.98, -22.92) * mm, "end": v(72.51, -24.35) * mm});
            skLineSegment(sketch, "E47.3.42.0", {"start": v(83.92, -28.06) * mm, "end": v(72.51, -24.35) * mm});
            skLineSegment(sketch, "E47.6.42.0", {"start": v(84.39, -26.63) * mm, "end": v(72.98, -22.92) * mm});
            skLineSegment(sketch, "E47.9.42.0", {"start": v(84.39, -26.63) * mm, "end": v(83.92, -28.06) * mm});
            skLineSegment(sketch, "E47.1.43.0", {"start": v(74.97, -15.17) * mm, "end": v(74.66, -16.64) * mm});
            skLineSegment(sketch, "E47.3.43.0", {"start": v(86.4, -19.13) * mm, "end": v(74.66, -16.64) * mm});
            skLineSegment(sketch, "E47.6.43.0", {"start": v(86.7, -17.66) * mm, "end": v(74.97, -15.17) * mm});
            skLineSegment(sketch, "E47.9.43.0", {"start": v(86.7, -17.66) * mm, "end": v(86.4, -19.13) * mm});
            skLineSegment(sketch, "E47.1.44.0", {"start": v(76.15, -7.25) * mm, "end": v(75.99, -8.74) * mm});
            skLineSegment(sketch, "E47.3.44.0", {"start": v(87.92, -10) * mm, "end": v(75.99, -8.74) * mm});
            skLineSegment(sketch, "E47.6.44.0", {"start": v(88.08, -8.5) * mm, "end": v(76.15, -7.25) * mm});
            skLineSegment(sketch, "E47.9.44.0", {"start": v(88.08, -8.5) * mm, "end": v(87.92, -10) * mm});
            skLineSegment(sketch, "E47.1.45.0", {"start": v(76.49, 0.75) * mm, "end": v(76.49, -0.75) * mm});
            skLineSegment(sketch, "E47.3.45.0", {"start": v(88.49, -0.75) * mm, "end": v(76.49, -0.75) * mm});
            skLineSegment(sketch, "E47.6.45.0", {"start": v(88.49, 0.75) * mm, "end": v(76.49, 0.75) * mm});
            skLineSegment(sketch, "E47.9.45.0", {"start": v(88.49, 0.75) * mm, "end": v(88.49, -0.75) * mm});
            skLineSegment(sketch, "E47.1.46.0", {"start": v(75.99, 8.74) * mm, "end": v(76.15, 7.25) * mm});
            skLineSegment(sketch, "E47.3.46.0", {"start": v(88.08, 8.5) * mm, "end": v(76.15, 7.25) * mm});
            skLineSegment(sketch, "E47.6.46.0", {"start": v(87.92, 10) * mm, "end": v(75.99, 8.74) * mm});
            skLineSegment(sketch, "E47.9.46.0", {"start": v(87.92, 10) * mm, "end": v(88.08, 8.5) * mm});
            skLineSegment(sketch, "E47.1.47.0", {"start": v(74.66, 16.64) * mm, "end": v(74.97, 15.17) * mm});
            skLineSegment(sketch, "E47.3.47.0", {"start": v(86.7, 17.66) * mm, "end": v(74.97, 15.17) * mm});
            skLineSegment(sketch, "E47.6.47.0", {"start": v(86.4, 19.13) * mm, "end": v(74.66, 16.64) * mm});
            skLineSegment(sketch, "E47.9.47.0", {"start": v(86.4, 19.13) * mm, "end": v(86.7, 17.66) * mm});
            skLineSegment(sketch, "E47.1.48.0", {"start": v(72.51, 24.35) * mm, "end": v(72.98, 22.92) * mm});
            skLineSegment(sketch, "E47.3.48.0", {"start": v(84.39, 26.63) * mm, "end": v(72.98, 22.92) * mm});
            skLineSegment(sketch, "E47.6.48.0", {"start": v(83.92, 28.06) * mm, "end": v(72.51, 24.35) * mm});
            skLineSegment(sketch, "E47.9.48.0", {"start": v(83.92, 28.06) * mm, "end": v(84.39, 26.63) * mm});
            skLineSegment(sketch, "E47.1.49.0", {"start": v(69.57, 31.8) * mm, "end": v(70.18, 30.43) * mm});
            skLineSegment(sketch, "E47.3.49.0", {"start": v(81.14, 35.3) * mm, "end": v(70.18, 30.43) * mm});
            skLineSegment(sketch, "E47.6.49.0", {"start": v(80.53, 36.68) * mm, "end": v(69.57, 31.8) * mm});
            skLineSegment(sketch, "E47.9.49.0", {"start": v(80.53, 36.68) * mm, "end": v(81.14, 35.3) * mm});
            skLineSegment(sketch, "E47.1.50.0", {"start": v(65.86, 38.9) * mm, "end": v(66.61, 37.6) * mm});
            skLineSegment(sketch, "E47.3.50.0", {"start": v(77, 43.6) * mm, "end": v(66.61, 37.6) * mm});
            skLineSegment(sketch, "E47.6.50.0", {"start": v(76.26, 44.9) * mm, "end": v(65.86, 38.9) * mm});
            skLineSegment(sketch, "E47.9.50.0", {"start": v(76.26, 44.9) * mm, "end": v(77, 43.6) * mm});
            skLineSegment(sketch, "E47.1.51.0", {"start": v(61.44, 45.56) * mm, "end": v(62.32, 44.35) * mm});
            skLineSegment(sketch, "E47.3.51.0", {"start": v(72.03, 51.4) * mm, "end": v(62.32, 44.35) * mm});
            skLineSegment(sketch, "E47.6.51.0", {"start": v(71.15, 52.62) * mm, "end": v(61.44, 45.56) * mm});
            skLineSegment(sketch, "E47.9.51.0", {"start": v(71.15, 52.62) * mm, "end": v(72.03, 51.4) * mm});
            skLineSegment(sketch, "E47.1.52.0", {"start": v(56.34, 51.74) * mm, "end": v(57.34, 50.62) * mm});
            skLineSegment(sketch, "E47.3.52.0", {"start": v(66.26, 58.65) * mm, "end": v(57.34, 50.62) * mm});
            skLineSegment(sketch, "E47.6.52.0", {"start": v(65.26, 59.77) * mm, "end": v(56.34, 51.74) * mm});
            skLineSegment(sketch, "E47.9.52.0", {"start": v(65.26, 59.77) * mm, "end": v(66.26, 58.65) * mm});
            skLineSegment(sketch, "E47.1.53.0", {"start": v(50.62, 57.34) * mm, "end": v(51.74, 56.34) * mm});
            skLineSegment(sketch, "E47.3.53.0", {"start": v(59.77, 65.26) * mm, "end": v(51.74, 56.34) * mm});
            skLineSegment(sketch, "E47.6.53.0", {"start": v(58.65, 66.26) * mm, "end": v(50.62, 57.34) * mm});
            skLineSegment(sketch, "E47.9.53.0", {"start": v(58.65, 66.26) * mm, "end": v(59.77, 65.26) * mm});
            skLineSegment(sketch, "E47.1.54.0", {"start": v(44.35, 62.32) * mm, "end": v(45.56, 61.44) * mm});
            skLineSegment(sketch, "E47.3.54.0", {"start": v(52.62, 71.15) * mm, "end": v(45.56, 61.44) * mm});
            skLineSegment(sketch, "E47.6.54.0", {"start": v(51.4, 72.03) * mm, "end": v(44.35, 62.32) * mm});
            skLineSegment(sketch, "E47.9.54.0", {"start": v(51.4, 72.03) * mm, "end": v(52.62, 71.15) * mm});
            skLineSegment(sketch, "E47.1.55.0", {"start": v(37.6, 66.61) * mm, "end": v(38.9, 65.86) * mm});
            skLineSegment(sketch, "E47.3.55.0", {"start": v(44.9, 76.26) * mm, "end": v(38.9, 65.86) * mm});
            skLineSegment(sketch, "E47.6.55.0", {"start": v(43.6, 77) * mm, "end": v(37.6, 66.61) * mm});
            skLineSegment(sketch, "E47.9.55.0", {"start": v(43.6, 77) * mm, "end": v(44.9, 76.26) * mm});
            skLineSegment(sketch, "E47.1.56.0", {"start": v(30.43, 70.18) * mm, "end": v(31.8, 69.57) * mm});
            skLineSegment(sketch, "E47.3.56.0", {"start": v(36.68, 80.53) * mm, "end": v(31.8, 69.57) * mm});
            skLineSegment(sketch, "E47.6.56.0", {"start": v(35.3, 81.14) * mm, "end": v(30.43, 70.18) * mm});
            skLineSegment(sketch, "E47.9.56.0", {"start": v(35.3, 81.14) * mm, "end": v(36.68, 80.53) * mm});
            skLineSegment(sketch, "E47.1.57.0", {"start": v(22.92, 72.98) * mm, "end": v(24.35, 72.51) * mm});
            skLineSegment(sketch, "E47.3.57.0", {"start": v(28.06, 83.92) * mm, "end": v(24.35, 72.51) * mm});
            skLineSegment(sketch, "E47.6.57.0", {"start": v(26.63, 84.39) * mm, "end": v(22.92, 72.98) * mm});
            skLineSegment(sketch, "E47.9.57.0", {"start": v(26.63, 84.39) * mm, "end": v(28.06, 83.92) * mm});
            skLineSegment(sketch, "E47.1.58.0", {"start": v(15.17, 74.97) * mm, "end": v(16.64, 74.66) * mm});
            skLineSegment(sketch, "E47.3.58.0", {"start": v(19.13, 86.4) * mm, "end": v(16.64, 74.66) * mm});
            skLineSegment(sketch, "E47.6.58.0", {"start": v(17.66, 86.7) * mm, "end": v(15.17, 74.97) * mm});
            skLineSegment(sketch, "E47.9.58.0", {"start": v(17.66, 86.7) * mm, "end": v(19.13, 86.4) * mm});
            skLineSegment(sketch, "E47.1.59.0", {"start": v(7.25, 76.15) * mm, "end": v(8.74, 75.99) * mm});
            skLineSegment(sketch, "E47.3.59.0", {"start": v(10, 87.92) * mm, "end": v(8.74, 75.99) * mm});
            skLineSegment(sketch, "E47.6.59.0", {"start": v(8.5, 88.08) * mm, "end": v(7.25, 76.15) * mm});
            skLineSegment(sketch, "E47.9.59.0", {"start": v(8.5, 88.08) * mm, "end": v(10, 87.92) * mm});
            skSolve(sketch);
        }
        {
            var Q0;
            Q0 = qSketchRegion(id + "F27", true);
            extrude(context, id + "F28", {"entities" : qUnion([Q0]), "operationType" : NewBodyOperationType.REMOVE, "oppositeDirection" : true, "depth" : 0.2 * mm, "offsetDistance" : 25 * mm});
        }
        {
            var Q0;
            Q0=makeQuery(id+"F26.boolean.opBoolean","COPY",FACE,{"derivedFrom":makeQuery(id+"F26.opExtrude","CAP_FACE",FACE,{"disambiguationData":[OSD([sQuery(id+"F25.wireOp",EDGE,"E41.bottom"),sQuery(id+"F25.wireOp",EDGE,"E41.top"),sQuery(id+"F25.wireOp",EDGE,"E41.left"),sQuery(id+"F25.wireOp",EDGE,"E41.right")])],"isStart":false})});
            extrude(context, id + "F29", {"entities" : qUnion([Q0]), "depth" : 1 * mm, "offsetDistance" : 25 * mm});
        }
        {
            var Q0;
            Q0=makeQuery(id+"F28.boolean.opBoolean","COPY",FACE,{"derivedFrom":makeQuery(id+"F28.opExtrude","CAP_FACE",FACE,{"disambiguationData":[OSD([sQuery(id+"F27.wireOp",EDGE,"E47.1.59.0"),sQuery(id+"F27.wireOp",EDGE,"E47.3.59.0"),sQuery(id+"F27.wireOp",EDGE,"E47.6.59.0"),sQuery(id+"F27.wireOp",EDGE,"E47.9.59.0")])],"isStart":false})});
            extrude(context, id + "F30", {"entities" : qUnion([Q0]), "depth" : 0.4 * mm, "offsetDistance" : 25 * mm});
        }
        {
            var Q0;
            Q0=makeQuery(id+"F24.opExtrude","CAP_FACE",FACE,{"disambiguationData":[OSD([sQuery(id+"F23.wireOp",EDGE,"E39.0.0"),sQuery(id+"F23.wireOp",EDGE,"E40")])],"isStart":true});
            var sketch = newSketch(context, id + "F31", { "sketchPlane" : qUnion([Q0])});
            skCircle(sketch, "E48.0", {"center": v(0, 0) * mm, "radius": 5 * mm});
            skCircle(sketch, "E49.0", {"center": v(0, 0) * mm, "radius": 3 * mm});
            skSolve(sketch);
        }
        {
            var Q0;
            Q0 = qSketchRegion(id + "F31", true);
            extrude(context, id + "F32", {"entities" : qUnion([Q0]), "operationType" : NewBodyOperationType.ADD, "depth" : 5 * mm, "offsetDistance" : 25 * mm});
        }
        {
            var Q0;
            Q0=makeQuery(id+"F32.opExtrude","CAP_FACE",FACE,{"disambiguationData":[OSD([sQuery(id+"F31.wireOp",EDGE,"E48.0"),sQuery(id+"F31.wireOp",EDGE,"E49.0")])],"isStart":false});
            var sketch = newSketch(context, id + "F33", { "sketchPlane" : qUnion([Q0])});
            skCircle(sketch, "E50.0", {"center": v(0, 0) * mm, "radius": 3 * mm});
            skCircle(sketch, "E51.0", {"center": v(0, 0) * mm, "radius": 5 * mm});
            skLineSegment(sketch, "E52", {"start": v(0, 50) * mm, "end": v(1.5, 50) * mm});
            skLineSegment(sketch, "E53", {"start": v(1.5, 50) * mm, "end": v(3, 4) * mm});
            skLineSegment(sketch, "E54.MirrorCS", {"start": v(0, 50) * mm, "end": v(-1.5, 50) * mm});
            skLineSegment(sketch, "E55.MirrorCS", {"start": v(-1.5, 50) * mm, "end": v(-3, 4) * mm});
            skSolve(sketch);
        }
        {
            var Q0;
            Q0 = qSketchRegion(id + "F33", true);
            extrude(context, id + "F34", {"entities" : qUnion([Q0]), "operationType" : NewBodyOperationType.ADD, "depth" : 1 * mm, "offsetDistance" : 25 * mm});
        }
        {
            var Q0;
            Q0=makeQuery(id+"F6.opExtrude","CAP_FACE",FACE,{"disambiguationData":[OSD([sQuery(id+"F0.wireOp",EDGE,"E0")])],"isStart":false});
            var sketch = newSketch(context, id + "F35", { "sketchPlane" : qUnion([Q0])});
            skCircle(sketch, "E56", {"center": v(0, 0) * mm, "radius": 5 * mm});
            skLineSegment(sketch, "E57", {"start": v(0, 80) * mm, "end": v(0.5, 80) * mm});
            skLineSegment(sketch, "E58", {"start": v(0.5, 80) * mm, "end": v(2, 4.58) * mm});
            skLineSegment(sketch, "E59.MirrorCS", {"start": v(0, 80) * mm, "end": v(-0.5, 80) * mm});
            skLineSegment(sketch, "E60.MirrorCS", {"start": v(-0.5, 80) * mm, "end": v(-2, 4.58) * mm});
            skSolve(sketch);
        }
        {
            var Q0;
            Q0 = qSketchRegion(id + "F35", true);
            extrude(context, id + "F36", {"entities" : qUnion([Q0]), "operationType" : NewBodyOperationType.ADD, "oppositeDirection" : true, "depth" : 1 * mm, "offsetDistance" : 25 * mm});
        }
    });
